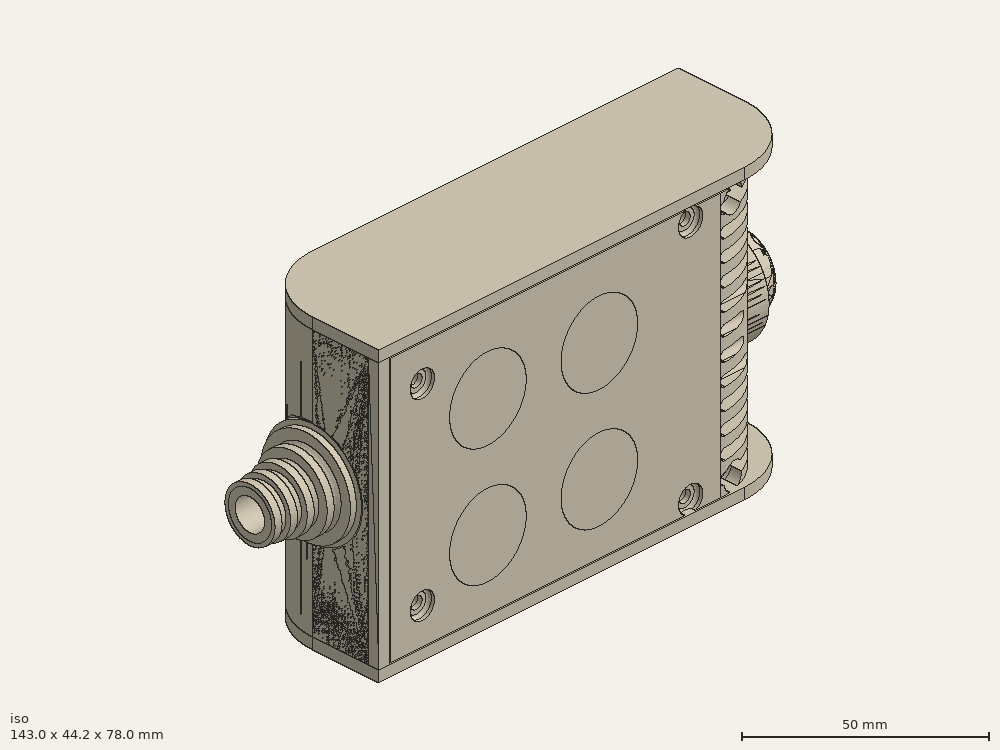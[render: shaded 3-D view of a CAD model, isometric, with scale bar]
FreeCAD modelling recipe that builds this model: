
FCSTD DOCUMENT  (FreeCAD 0.19R0.19.2)
Label: enclosure_126
License: All rights reserved
LicenseURL: http://en.wikipedia.org/wiki/All_rights_reserved
objects: Part::Feature×72, Part::Revolution×72, Part::MultiFuse×61, Sketcher::SketchObject×37, Part::Fillet×26, Part::Extrusion×25, Part::Cut×25, Part::Cylinder×22, Part::Box×12, App::MeasureDistance×4
note: 352 computed .brp shape members not serialized (recipe doc carries the construction recipe); baked Part::Feature solids carry a one-line shape summary decoded from their .brp

FEATURE [Sketcher::SketchObject] Sketch  label="topSketch"
  FullyConstrained = true
  sketch-geometry (20):
    g0: LineSegment StartX=5.58133e-06 StartY=3 StartZ=0 EndX=5.58133e-06 EndY=19 EndZ=0
    g1: ArcOfCircle CenterX=19 CenterY=19 CenterZ=0 NormalX=0 NormalY=0 NormalZ=1 AngleXU=0 Radius=19 StartAngle=1.5708 EndAngle=3.14159
    g2: ArcOfCircle CenterX=19 CenterY=19 CenterZ=0 NormalX=0 NormalY=0 NormalZ=1 AngleXU=0 Radius=16 StartAngle=1.5708 EndAngle=3.14159
    g3: LineSegment StartX=114 StartY=35 StartZ=0 EndX=19 EndY=35 EndZ=0
    g4: LineSegment StartX=5.58133e-06 StartY=3 StartZ=0 EndX=5.58133e-06 EndY=0 EndZ=0
    g5: LineSegment StartX=3.00001 StartY=0 StartZ=0 EndX=5.58133e-06 EndY=0 EndZ=0
    g6: LineSegment StartX=3.00001 StartY=19 StartZ=0 EndX=3.00001 EndY=0 EndZ=0
    g7: LineSegment StartX=19 StartY=38 StartZ=0 EndX=124 EndY=38 EndZ=0
    g8: LineSegment StartX=124 StartY=38 StartZ=0 EndX=124 EndY=19 EndZ=0
    g9: Circle CenterX=119 CenterY=35 CenterZ=0 NormalX=0 NormalY=0 NormalZ=1 AngleXU=0 Radius=1
    g10: Circle CenterX=121 CenterY=35 CenterZ=0 NormalX=0 NormalY=0 NormalZ=1 AngleXU=0 Radius=1
    g11: Circle CenterX=121 CenterY=33 CenterZ=0 NormalX=0 NormalY=0 NormalZ=1 AngleXU=0 Radius=1
    g12: BSplineCurve PolesCount=3 KnotsCount=2 Degree=2 IsPeriodic=0
    g13: GeomPoint X=119 Y=35 Z=0
    g14: GeomPoint X=121 Y=33 Z=0
    g15: LineSegment StartX=119 StartY=35 StartZ=0 EndX=114 EndY=35 EndZ=0
    g16: LineSegment StartX=121 StartY=33 StartZ=0 EndX=121 EndY=19 EndZ=0
    g17: ArcOfCircle CenterX=105 CenterY=19 CenterZ=0 NormalX=0 NormalY=0 NormalZ=1 AngleXU=0 Radius=19 StartAngle=5.7297 EndAngle=6.28319
    g18: ArcOfCircle CenterX=105 CenterY=19 CenterZ=0 NormalX=0 NormalY=0 NormalZ=1 AngleXU=0 Radius=16 StartAngle=5.60905 EndAngle=6.28319
    g19: LineSegment StartX=117.5 StartY=9.01251 StartZ=0 EndX=121.163 EndY=9.0125 EndZ=0
  constraints (44):
    c: Vertical(g0)
    c: Block(g0)
    c: Coincident(g1,g0)
    c: Block(g1)
    c: Coincident(g2,g1)
    c: Block(g2)
    c: Coincident(g3,g2)
    c: Horizontal(g3)
    c: Tangent(g3,g2)
    c: Coincident(g4,g0)
    c: Distance(g4) = 3
    c: Vertical(g4)
    c: Coincident(g5,g4)
    c: Horizontal(g5)
    c: Coincident(g6,g2)
    c: Coincident(g6,g5)
    c: Vertical(g6)
    c: Horizontal(g7)
    c: Distance(g7) = 105
    c: Coincident(g7,g1)
    c: Vertical(g8)
    c: Distance(g8) = 19
    c: Block(g3)
    c: Coincident(g8,g7)
    c: Weight(g9) = 1
    c: Equal(g9,g10)
    c: Equal(g9,g11)
    c: InternalAlignment(g9,g12)
    c: InternalAlignment(g10,g12)
    c: InternalAlignment(g11,g12)
    c: InternalAlignment(g13,g12)
    c: InternalAlignment(g14,g12)
    c: Block(g12)
    c: Coincident(g15,g12)
    c: Coincident(g15,g3)
    c: Horizontal(g15)
    c: Coincident(g16,g12)
    c: Vertical(g16)
    c: Distance(g16) = 14
    c: Block(g17)
    c: Coincident(g18,g17)
    c: Block(g18)
    c: Coincident(g19,g18)
    c: Coincident(g19,g17)
FEATURE [Sketcher::SketchObject] Sketch001  label="bottomSketch"
  FullyConstrained = true
  sketch-geometry (32):
    g0: LineSegment StartX=3.3 StartY=-6.03275e-07 StartZ=0 EndX=98 EndY=-6.03275e-07 EndZ=0
    g1: ArcOfCircle CenterX=98 CenterY=19 CenterZ=0 NormalX=0 NormalY=0 NormalZ=1 AngleXU=0 Radius=19 StartAngle=4.71239 EndAngle=5.71103
    g2: LineSegment StartX=6.3 StartY=8 StartZ=0 EndX=3.3 EndY=8 EndZ=0
    g3: LineSegment StartX=3.3 StartY=8 StartZ=0 EndX=3.3 EndY=-6.03275e-07 EndZ=0
    g4: ArcOfCircle CenterX=8.3 CenterY=5 CenterZ=0 NormalX=0 NormalY=0 NormalZ=1 AngleXU=0 Radius=2 StartAngle=3.14159 EndAngle=4.71239
    g5: LineSegment StartX=6.3 StartY=8 StartZ=0 EndX=6.3 EndY=5 EndZ=0
    g6: ArcOfCircle CenterX=98 CenterY=19 CenterZ=0 NormalX=0 NormalY=0 NormalZ=1 AngleXU=0 Radius=12.7 StartAngle=4.71239 EndAngle=6.28319
    g7: LineSegment StartX=94.7 StartY=3 StartZ=0 EndX=8.3 EndY=3 EndZ=0
    g8-g12: Circle x5 (B-spline internal-alignment scaffolding for g13; pole/knot coordinates omitted)
    g13: BSplineCurve PolesCount=5 KnotsCount=3 Degree=3 IsPeriodic=0
    g14: GeomPoint X=98 Y=6.3 Z=0
    g15: GeomPoint X=96.3938 Y=4.71946 Z=0
    g16: GeomPoint X=94.7 Y=3 Z=0
    g17-g23: Circle x7 (B-spline internal-alignment scaffolding for g24; pole/knot coordinates omitted)
    g24: BSplineCurve PolesCount=7 KnotsCount=5 Degree=3 IsPeriodic=0
    g25-g29: GeomPoint x5 (B-spline internal-alignment scaffolding for g24; pole/knot coordinates omitted)
    g30: ArcOfCircle CenterX=98 CenterY=19 CenterZ=0 NormalX=0 NormalY=0 NormalZ=1 AngleXU=0 Radius=15.7 StartAngle=5.81226 EndAngle=6.28319
    g31: LineSegment StartX=110.7 StartY=19 StartZ=0 EndX=113.7 EndY=19 EndZ=0
  constraints (41):
    c: Horizontal(g0)
    c: Coincident(g1,g0)
    c: Block(g1)
    c: Horizontal(g2)
    c: Distance(g2) = 3
    c: Coincident(g3,g2)
    c: Vertical(g3)
    c: Coincident(g3,g0)
    c: Block(g4)
    c: Block(g2)
    c: Coincident(g5,g2)
    c: Coincident(g5,g4)
    c: Vertical(g5)
    c: Coincident(g6,g1)
    c: Block(g6)
    c: Coincident(g7,g4)
    c: Horizontal(g7)
    c: Block(g0)
    c: Block(g7)
    c: Block(g3)
    c: Coincident(g13,g6)
    c: Weight(g8) = 1
    c: Equal(g8, g9-g12) x4
    c: Coincident(g13,g7)
    c: InternalAlignment(g8-g12 -> g13) x5
    c: InternalAlignment(g14,g13)
    c: InternalAlignment(g15,g13)
    c: InternalAlignment(g16,g13)
    c: Block(g13)
    c: Weight(g17) = 1
    c: Equal(g17, g18-g23) x6
    c: Coincident(g24,g1)
    c: InternalAlignment(g17-g23 -> g24) x7
    c: InternalAlignment(g25-g29 -> g24) x5
    c: Block(g24)
    c: Coincident(g30,g24)
    c: Coincident(g31,g6)
    c: Coincident(g31,g30)
    c: Horizontal(g31)
    c: Block(g31)
    c: Block(g30)
FEATURE [Part::Extrusion] Extrude  label="top"
  Base = -> Sketch
  Dir = (0,0,1)
  DirMode = 2
  FaceMakerClass = Part::FaceMakerBullseye
  LengthFwd = 72
  LengthRev = 0
  Solid = true
  Symmetric = false
FEATURE [Part::Extrusion] Extrude001  label="bottom"
  Base = -> Sketch001
  Dir = (0,0,1)
  DirMode = 2
  FaceMakerClass = Part::FaceMakerBullseye
  LengthFwd = 71.4
  LengthRev = 0
  Placement = pos=(0,0,0.3) rot=(0,0,1;0rad)
  Solid = true
  Symmetric = false
FEATURE [Sketcher::SketchObject] Sketch002  label="topSketch001"
  FullyConstrained = true
  sketch-geometry (6):
    g0: ArcOfCircle CenterX=19 CenterY=19 CenterZ=0 NormalX=0 NormalY=0 NormalZ=1 AngleXU=0 Radius=19 StartAngle=1.5708 EndAngle=3.14159
    g1: LineSegment StartX=5.22862e-06 StartY=19 StartZ=0 EndX=5.22862e-06 EndY=1.19904e-11 EndZ=0
    g2: LineSegment StartX=19 StartY=38 StartZ=0 EndX=124 EndY=38 EndZ=0
    g3: LineSegment StartX=5.22862e-06 StartY=1.19904e-11 StartZ=0 EndX=105 EndY=1.19904e-11 EndZ=0
    g4: ArcOfCircle CenterX=105 CenterY=19 CenterZ=0 NormalX=0 NormalY=0 NormalZ=1 AngleXU=0 Radius=19 StartAngle=4.71239 EndAngle=6.28319
    g5: LineSegment StartX=124 StartY=38 StartZ=0 EndX=124 EndY=19 EndZ=0
  constraints (16):
    c: Block(g0)
    c: Coincident(g1,g0)
    c: Vertical(g1)
    c: Horizontal(g2)
    c: Distance(g2) = 105
    c: Coincident(g2,g0)
    c: Distance(g1) = 19
    c: Coincident(g3,g1)
    c: Horizontal(g3)
    c: Distance(g3) = 105
    c: Block(g4)
    c: Coincident(g4,g3)
    c: Coincident(g5,g2)
    c: Coincident(g5,g4)
    c: Vertical(g5)
    c: Distance(g5) = 19
FEATURE [Part::Extrusion] Extrude002  label="sideA"
  Base = -> Sketch002
  Dir = (0,0,1)
  DirMode = 2
  FaceMakerClass = Part::FaceMakerBullseye
  LengthFwd = 3
  LengthRev = 0
  Placement = pos=(0,0,-3) rot=(0,0,1;0rad)
  Solid = true
  Symmetric = false
FEATURE [Sketcher::SketchObject] Sketch003  label="topSketch002"
  FullyConstrained = true
  sketch-geometry (6):
    g0: LineSegment StartX=19 StartY=38 StartZ=0 EndX=117 EndY=38 EndZ=0
    g1: ArcOfCircle CenterX=19 CenterY=19 CenterZ=0 NormalX=0 NormalY=0 NormalZ=1 AngleXU=0 Radius=19 StartAngle=1.5708 EndAngle=3.14159
    g2: LineSegment StartX=117 StartY=38 StartZ=0 EndX=117 EndY=19 EndZ=0
    g3: LineSegment StartX=98 StartY=1.0161e-12 StartZ=0 EndX=5.22862e-06 EndY=1.0161e-12 EndZ=0
    g4: LineSegment StartX=5.22862e-06 StartY=19 StartZ=0 EndX=5.22862e-06 EndY=1.0161e-12 EndZ=0
    g5: ArcOfCircle CenterX=98 CenterY=19 CenterZ=0 NormalX=0 NormalY=0 NormalZ=1 AngleXU=0 Radius=19 StartAngle=4.71239 EndAngle=6.28319
  constraints (16):
    c: Horizontal(g0)
    c: Distance(g0) = 98
    c: Coincident(g1,g0)
    c: Block(g1)
    c: Coincident(g2,g0)
    c: Vertical(g2)
    c: Distance(g2) = 19
    c: Horizontal(g3)
    c: Coincident(g4,g1)
    c: Vertical(g4)
    c: Coincident(g3,g4)
    c: Block(g3)
    c: Coincident(g5,g2)
    c: Coincident(g5,g3)
    c: Block(g0)
    c: Block(g5)
FEATURE [Sketcher::SketchObject] Sketch004
  FullyConstrained = true
  MapMode = 3
  Placement = pos=(0,0,0) rot=(1,0,0;1.5708rad)
  Support = -> [Extrude]
  sketch-geometry (8):
    g0: Circle CenterX=80.351 CenterY=-67.6202 CenterZ=0 NormalX=0 NormalY=0 NormalZ=1 AngleXU=0 Radius=2
    g1: Circle CenterX=80.351 CenterY=-67.6202 CenterZ=0 NormalX=0 NormalY=0 NormalZ=1 AngleXU=0 Radius=3
    g2: Circle CenterX=80.351 CenterY=-4.92017 CenterZ=0 NormalX=0 NormalY=0 NormalZ=1 AngleXU=0 Radius=2
    g3: Circle CenterX=80.351 CenterY=-4.92017 CenterZ=0 NormalX=0 NormalY=0 NormalZ=1 AngleXU=0 Radius=3
    g4: Circle CenterX=23.851 CenterY=-4.92017 CenterZ=0 NormalX=0 NormalY=0 NormalZ=1 AngleXU=0 Radius=2
    g5: Circle CenterX=23.851 CenterY=-4.92017 CenterZ=0 NormalX=0 NormalY=0 NormalZ=1 AngleXU=0 Radius=3
    g6: Circle CenterX=23.851 CenterY=-67.6202 CenterZ=0 NormalX=0 NormalY=0 NormalZ=1 AngleXU=0 Radius=2
    g7: Circle CenterX=23.851 CenterY=-67.6202 CenterZ=0 NormalX=0 NormalY=0 NormalZ=1 AngleXU=0 Radius=3
  constraints (8):
    c: Block(g3)
    c: Block(g2)
    c: Block(g1)
    c: Block(g0)
    c: Block(g6)
    c: Block(g7)
    c: Block(g4)
    c: Block(g5)
FEATURE [Part::Extrusion] Extrude004
  Base = -> Sketch004
  Dir = (0,-1,2e-16)
  DirMode = 2
  FaceMakerClass = Part::FaceMakerBullseye
  LengthFwd = 6
  LengthRev = 0
  Placement = pos=(0,9,0) rot=(0,0,1;0rad)
  Solid = true
  Symmetric = false
FEATURE [Sketcher::SketchObject] Sketch005
  FullyConstrained = true
  MapMode = 3
  Placement = pos=(0,0,0) rot=(1,0,0;1.5708rad)
  Support = -> [Extrude]
  sketch-geometry (8):
    g0: Circle CenterX=80.351 CenterY=-67.6202 CenterZ=0 NormalX=0 NormalY=0 NormalZ=1 AngleXU=0 Radius=3
    g1: Circle CenterX=80.351 CenterY=-4.92017 CenterZ=0 NormalX=0 NormalY=0 NormalZ=1 AngleXU=0 Radius=3
    g2: Circle CenterX=23.851 CenterY=-4.92017 CenterZ=0 NormalX=0 NormalY=0 NormalZ=1 AngleXU=0 Radius=3
    g3: Circle CenterX=23.851 CenterY=-67.6202 CenterZ=0 NormalX=0 NormalY=0 NormalZ=1 AngleXU=0 Radius=3
    g4: Circle CenterX=23.851 CenterY=-67.6202 CenterZ=0 NormalX=0 NormalY=0 NormalZ=1 AngleXU=0 Radius=5
    g5: Circle CenterX=80.351 CenterY=-67.6202 CenterZ=0 NormalX=0 NormalY=0 NormalZ=1 AngleXU=0 Radius=5
    g6: Circle CenterX=23.851 CenterY=-4.92017 CenterZ=0 NormalX=0 NormalY=0 NormalZ=1 AngleXU=0 Radius=5
    g7: Circle CenterX=80.351 CenterY=-4.92017 CenterZ=0 NormalX=0 NormalY=0 NormalZ=1 AngleXU=0 Radius=5
  constraints (8):
    c: Block(g1)
    c: Block(g0)
    c: Block(g3)
    c: Block(g2)
    c: Block(g5)
    c: Block(g4)
    c: Block(g6)
    c: Block(g7)
FEATURE [Part::Extrusion] Extrude005
  Base = -> Sketch005
  Dir = (0,-1,2e-16)
  DirMode = 2
  FaceMakerClass = Part::FaceMakerBullseye
  LengthFwd = 2
  LengthRev = 0
  Solid = true
  Symmetric = false
FEATURE [Sketcher::SketchObject] Sketch006
  FullyConstrained = true
  MapMode = 3
  Placement = pos=(0,0,0) rot=(1,0,0;1.5708rad)
  sketch-geometry (8):
    g0: Circle CenterX=80.351 CenterY=-67.6202 CenterZ=0 NormalX=0 NormalY=0 NormalZ=1 AngleXU=0 Radius=3
    g1: Circle CenterX=80.351 CenterY=-4.92017 CenterZ=0 NormalX=0 NormalY=0 NormalZ=1 AngleXU=0 Radius=3
    g2: Circle CenterX=23.851 CenterY=-4.92017 CenterZ=0 NormalX=0 NormalY=0 NormalZ=1 AngleXU=0 Radius=3
    g3: Circle CenterX=23.851 CenterY=-67.6202 CenterZ=0 NormalX=0 NormalY=0 NormalZ=1 AngleXU=0 Radius=3
    g4: Circle CenterX=23.851 CenterY=-67.6202 CenterZ=0 NormalX=0 NormalY=0 NormalZ=1 AngleXU=0 Radius=5
    g5: Circle CenterX=80.351 CenterY=-67.6202 CenterZ=0 NormalX=0 NormalY=0 NormalZ=1 AngleXU=0 Radius=5
    g6: Circle CenterX=23.851 CenterY=-4.92017 CenterZ=0 NormalX=0 NormalY=0 NormalZ=1 AngleXU=0 Radius=5
    g7: Circle CenterX=80.351 CenterY=-4.92017 CenterZ=0 NormalX=0 NormalY=0 NormalZ=1 AngleXU=0 Radius=5
  constraints (8):
    c: Block(g1)
    c: Block(g0)
    c: Block(g3)
    c: Block(g2)
    c: Block(g5)
    c: Block(g4)
    c: Block(g6)
    c: Block(g7)
FEATURE [Part::Extrusion] Extrude007
  Base = -> Sketch006
  Dir = (0,-1,2e-16)
  DirMode = 2
  FaceMakerClass = Part::FaceMakerBullseye
  LengthFwd = 2
  LengthRev = 0
  Solid = true
  Symmetric = false
FEATURE [Part::Fillet] Fillet
  Base = -> Extrude007
  Edges = 4 edges r=1.99: [Edge6,Edge12,Edge18,Edge24]
FEATURE [Part::Cut] Cut
  Base = -> Extrude005
  Placement = pos=(0,5,0) rot=(0,0,1;0rad)
  Tool = -> Fillet
FEATURE [Part::MultiFuse] Fusion  label="pCBScrews"
  Placement = pos=(-2.5,0,72.3) rot=(0,0,1;0rad)
  Shapes = -> [Extrude004,Cut]
FEATURE [App::MeasureDistance] Distance  label="Distance: 0.69 mm"
  Distance = 0.685967
  P1 = (24.0138,2.9647,0.3)
  P2 = (23.8901,3,-0.373787)
FEATURE [App::MeasureDistance] Distance001  label="Distance: 0.53 mm"
  Distance = 0.533607
  P1 = (80.2939,3,72.2334)
  P2 = (80.281,2.99661,71.7)
FEATURE [Part::Fillet] Fillet001
  Base = -> Extrude001
  Edges = 1 edges r=2.4: [Edge17]
FEATURE [Part::Fillet] Fillet002  label="bottom001"
  Base = -> Fillet001
  Edges = 1 edges r=2.4: [Edge36]
FEATURE [Part::Fillet] Fillet003  label="top001"
  Base = -> Extrude
  Edges = 1 edges r=2: [Edge1]
FEATURE [Sketcher::SketchObject] Sketch007
  FullyConstrained = true
  sketch-geometry (16):
    g0: LineSegment StartX=4 StartY=0 StartZ=0 EndX=4 EndY=2.4 EndZ=0
    g1: LineSegment StartX=4 StartY=2.4 StartZ=0 EndX=7 EndY=2.4 EndZ=0
    g2: LineSegment StartX=4 StartY=0 StartZ=0 EndX=5.7 EndY=0 EndZ=0
    g3: LineSegment StartX=5.7 StartY=0 StartZ=0 EndX=5.7 EndY=-5.6 EndZ=0
    g4-g8: Circle x5 (B-spline internal-alignment scaffolding for g9; pole/knot coordinates omitted)
    g9: BSplineCurve PolesCount=5 KnotsCount=3 Degree=3 IsPeriodic=0
    g10: GeomPoint X=7 Y=2.4 Z=0
    g11: GeomPoint X=10.4582 Y=-1.55472 Z=0
    g12: GeomPoint X=14 Y=-5.6 Z=0
    g13: LineSegment StartX=14 StartY=-5.6 StartZ=0 EndX=14 EndY=-14.1 EndZ=0
    g14: LineSegment StartX=14 StartY=-14.1 StartZ=0 EndX=6.5 EndY=-14.1 EndZ=0
    g15: LineSegment StartX=5.7 StartY=-5.6 StartZ=0 EndX=6.5 EndY=-14.1 EndZ=0
  constraints (28):
    c: Distance(g0) = 2.4
    c: Vertical(g0)
    c: Block(g0)
    c: Coincident(g1,g0)
    c: Horizontal(g1)
    c: Distance(g1) = 3
    c: Coincident(g2,g0)
    c: Horizontal(g2)
    c: Distance(g2) = 1.7
    c: Coincident(g3,g2)
    c: Vertical(g3)
    c: Distance(g3) = 5.6
    c: Coincident(g9,g1)
    c: Weight(g4) = 1
    c: Equal(g4, g5-g8) x4
    c: InternalAlignment(g4-g8 -> g9) x5
    c: InternalAlignment(g10,g9)
    c: InternalAlignment(g11,g9)
    c: InternalAlignment(g12,g9)
    c: Block(g9)
    c: Coincident(g13,g9)
    c: Vertical(g13)
    c: Distance(g13) = 8.5
    c: Coincident(g14,g13)
    c: Horizontal(g14)
    c: Distance(g14) = 7.5
    c: Coincident(g15,g3)
    c: Coincident(g15,g14)
FEATURE [Part::Feature] Face
  shape: bbox 10 x 16.5 x 2e-07 mm, 1 faces, 0 solids (baked)
FEATURE [Part::Revolution] Revolve  label="plugHousing"
  Angle = 360
  Axis = (0,1,0)
  Base = (0,0,0)
  FaceMakerClass = Part::FaceMakerBullseye
  Placement = pos=(0,0,36.15) rot=(0,0,1;0rad)
  Solid = false
  Source = -> Face
  Symmetric = false
FEATURE [Part::Feature] Face001
  shape: bbox 10 x 16.5 x 2e-07 mm, 1 faces, 0 solids (baked)
FEATURE [Part::Revolution] Revolve001  label="plugHousing001"
  Angle = 360
  Axis = (0,1,0)
  Base = (0,0,0)
  FaceMakerClass = Part::FaceMakerBullseye
  Placement = pos=(0,0,36.15) rot=(0,0,1;0rad)
  Solid = false
  Source = -> Face001
  Symmetric = false
FEATURE [Part::MultiFuse] Fusion001  label="plugHousing002"
  Placement = pos=(0,0,0) rot=(0,0,1;1.5708rad)
  Shapes = -> [Revolve001,Revolve]
FEATURE [Part::Feature] Face002
  shape: bbox 10 x 16.5 x 2e-07 mm, 1 faces, 0 solids (baked)
FEATURE [Part::Revolution] Revolve003  label="plugHousing005"
  Angle = 360
  Axis = (0,1,0)
  Base = (0,0,0)
  FaceMakerClass = Part::FaceMakerBullseye
  Placement = pos=(0,0,36.15) rot=(0,0,1;0rad)
  Solid = false
  Source = -> Face002
  Symmetric = false
FEATURE [Part::Feature] Face003
  shape: bbox 10 x 16.5 x 2e-07 mm, 1 faces, 0 solids (baked)
FEATURE [Part::Revolution] Revolve002  label="plugHousing003"
  Angle = 360
  Axis = (0,1,0)
  Base = (0,0,0)
  FaceMakerClass = Part::FaceMakerBullseye
  Placement = pos=(0,0,36.15) rot=(0,0,1;0rad)
  Solid = false
  Source = -> Face003
  Symmetric = false
FEATURE [Part::MultiFuse] Fusion002  label="plugHousing004"
  Placement = pos=(0,0,0) rot=(0,0,1;1.5708rad)
  Shapes = -> [Revolve002,Revolve003]
FEATURE [Part::MultiFuse] Fusion003  label="plugHousing006"
  Placement = pos=(0,19,0) rot=(0,0,1;3.14159rad)
  Shapes = -> [Fusion002,Fusion001]
FEATURE [Part::Feature] Face004
  shape: bbox 10 x 16.5 x 2e-07 mm, 1 faces, 0 solids (baked)
FEATURE [Part::Revolution] Revolve006  label="plugHousing010"
  Angle = 360
  Axis = (0,1,0)
  Base = (0,0,0)
  FaceMakerClass = Part::FaceMakerBullseye
  Placement = pos=(0,0,36.15) rot=(0,0,1;0rad)
  Solid = false
  Source = -> Face004
  Symmetric = false
FEATURE [Part::Feature] Face005
  shape: bbox 10 x 16.5 x 2e-07 mm, 1 faces, 0 solids (baked)
FEATURE [Part::Revolution] Revolve007  label="plugHousing011"
  Angle = 360
  Axis = (0,1,0)
  Base = (0,0,0)
  FaceMakerClass = Part::FaceMakerBullseye
  Placement = pos=(0,0,36.15) rot=(0,0,1;0rad)
  Solid = false
  Source = -> Face005
  Symmetric = false
FEATURE [Part::Feature] Face006
  shape: bbox 10 x 16.5 x 2e-07 mm, 1 faces, 0 solids (baked)
FEATURE [Part::Revolution] Revolve004  label="plugHousing007"
  Angle = 360
  Axis = (0,1,0)
  Base = (0,0,0)
  FaceMakerClass = Part::FaceMakerBullseye
  Placement = pos=(0,0,36.15) rot=(0,0,1;0rad)
  Solid = false
  Source = -> Face006
  Symmetric = false
FEATURE [Part::MultiFuse] Fusion004  label="plugHousing009"
  Placement = pos=(0,0,0) rot=(0,0,1;1.5708rad)
  Shapes = -> [Revolve004,Revolve007]
FEATURE [Part::Feature] Face007
  shape: bbox 10 x 16.5 x 2e-07 mm, 1 faces, 0 solids (baked)
FEATURE [Part::Revolution] Revolve005  label="plugHousing008"
  Angle = 360
  Axis = (0,1,0)
  Base = (0,0,0)
  FaceMakerClass = Part::FaceMakerBullseye
  Placement = pos=(0,0,36.15) rot=(0,0,1;0rad)
  Solid = false
  Source = -> Face007
  Symmetric = false
FEATURE [Part::MultiFuse] Fusion005  label="plugHousing012"
  Placement = pos=(0,0,0) rot=(0,0,1;1.5708rad)
  Shapes = -> [Revolve006,Revolve005]
FEATURE [Part::MultiFuse] Fusion006  label="plugHousing013"
  Placement = pos=(0,19,0) rot=(0,0,1;3.14159rad)
  Shapes = -> [Fusion005,Fusion004]
FEATURE [Part::MultiFuse] Fusion007  label="plugHousing014"
  Placement = pos=(122.621,0,-0.15) rot=(0,0,1;0rad)
  Shapes = -> [Fusion003,Fusion006]
FEATURE [Part::Cylinder] Cylinder002
  Angle = 360
  AttacherType = Attacher::AttachEngine3D
  Height = 20
  Placement = pos=(0,0,36.15) rot=(0,0,1;0rad)
  Radius = 4
FEATURE [Part::Cylinder] Cylinder003
  Angle = 360
  AttacherType = Attacher::AttachEngine3D
  Height = 10
  Placement = pos=(0,0,36.15) rot=(0,0,1;0rad)
  Radius = 4
FEATURE [Part::MultiFuse] Fusion009  label="removeToCreateHoleForPlugHousing"
  Placement = pos=(70,19,36.15) rot=(0,1,0;1.5708rad)
  Shapes = -> [Cylinder002,Cylinder003]
FEATURE [Part::Cylinder] Cylinder004
  Angle = 360
  AttacherType = Attacher::AttachEngine3D
  Height = 20
  Placement = pos=(0,0,36.15) rot=(0,0,1;0rad)
  Radius = 4
FEATURE [Part::Cylinder] Cylinder005
  Angle = 360
  AttacherType = Attacher::AttachEngine3D
  Height = 10
  Placement = pos=(0,0,36.15) rot=(0,0,1;0rad)
  Radius = 4
FEATURE [Part::MultiFuse] Fusion010  label="removeToCreateHoleForPlugHousing001"
  Placement = pos=(70,19,36.15) rot=(0,1,0;1.5708rad)
  Shapes = -> [Cylinder004,Cylinder005]
FEATURE [Part::Cut] Cut001
  Base = -> Fillet003
  Tool = -> Fusion010
FEATURE [Part::Cut] Cut002  label="Bottom"
  Base = -> Fillet002
  Tool = -> Fusion009
FEATURE [Part::Feature] Face008
  shape: bbox 10 x 16.5 x 2e-07 mm, 1 faces, 0 solids (baked)
FEATURE [Part::Revolution] Revolve011  label="plugHousing021"
  Angle = 360
  Axis = (0,1,0)
  Base = (0,0,0)
  FaceMakerClass = Part::FaceMakerBullseye
  Placement = pos=(0,0,36.15) rot=(0,0,1;0rad)
  Solid = false
  Source = -> Face008
  Symmetric = false
FEATURE [Part::Feature] Face009
  shape: bbox 10 x 16.5 x 2e-07 mm, 1 faces, 0 solids (baked)
FEATURE [Part::Revolution] Revolve012  label="plugHousing022"
  Angle = 360
  Axis = (0,1,0)
  Base = (0,0,0)
  FaceMakerClass = Part::FaceMakerBullseye
  Placement = pos=(0,0,36.15) rot=(0,0,1;0rad)
  Solid = false
  Source = -> Face009
  Symmetric = false
FEATURE [Part::Feature] Face010 .. Face013  x4 (patterned run collapsed; names and placements below)
  shape: bbox 10 x 16.5 x 2e-07 mm, 1 faces, 0 solids (baked)
FEATURE [Part::Revolution] Revolve015  label="plugHousing027"
  Angle = 360
  Axis = (0,1,0)
  Base = (0,0,0)
  FaceMakerClass = Part::FaceMakerBullseye
  Placement = pos=(0,0,36.15) rot=(0,0,1;0rad)
  Solid = false
  Source = -> Face013
  Symmetric = false
FEATURE [Part::Feature] Face014
  shape: bbox 10 x 16.5 x 2e-07 mm, 1 faces, 0 solids (baked)
FEATURE [Part::Feature] Face015
  shape: bbox 10 x 16.5 x 2e-07 mm, 1 faces, 0 solids (baked)
FEATURE [Part::Feature] Face016
  shape: bbox 10 x 16.5 x 2e-07 mm, 1 faces, 0 solids (baked)
FEATURE [Part::Revolution] Revolve019  label="plugHousing033"
  Angle = 360
  Axis = (0,1,0)
  Base = (0,0,0)
  FaceMakerClass = Part::FaceMakerBullseye
  Placement = pos=(0,0,36.15) rot=(0,0,1;0rad)
  Solid = false
  Source = -> Face016
  Symmetric = false
FEATURE [Part::Feature] Face017
  shape: bbox 10 x 16.5 x 2e-07 mm, 1 faces, 0 solids (baked)
FEATURE [Part::Revolution] Revolve020  label="plugHousing034"
  Angle = 360
  Axis = (0,1,0)
  Base = (0,0,0)
  FaceMakerClass = Part::FaceMakerBullseye
  Placement = pos=(0,0,36.15) rot=(0,0,1;0rad)
  Solid = false
  Source = -> Face017
  Symmetric = false
FEATURE [Part::Feature] Face018
  shape: bbox 10 x 16.5 x 2e-07 mm, 1 faces, 0 solids (baked)
FEATURE [Part::Revolution] Revolve016  label="plugHousing030"
  Angle = 360
  Axis = (0,1,0)
  Base = (0,0,0)
  FaceMakerClass = Part::FaceMakerBullseye
  Placement = pos=(0,0,36.15) rot=(0,0,1;0rad)
  Solid = false
  Source = -> Face018
  Symmetric = false
FEATURE [Part::MultiFuse] Fusion020  label="plugHousing038"
  Placement = pos=(0,0,0) rot=(0,0,1;1.5708rad)
  Shapes = -> [Revolve016,Revolve020]
FEATURE [Part::Feature] Face019
  shape: bbox 10 x 16.5 x 2e-07 mm, 1 faces, 0 solids (baked)
FEATURE [Part::Feature] Face020
  shape: bbox 10 x 16.5 x 2e-07 mm, 1 faces, 0 solids (baked)
FEATURE [Part::Revolution] Revolve017  label="plugHousing031"
  Angle = 360
  Axis = (0,1,0)
  Base = (0,0,0)
  FaceMakerClass = Part::FaceMakerBullseye
  Placement = pos=(0,0,36.15) rot=(0,0,1;0rad)
  Solid = false
  Source = -> Face020
  Symmetric = false
FEATURE [Part::MultiFuse] Fusion021  label="plugHousing039"
  Placement = pos=(0,0,0) rot=(0,0,1;1.5708rad)
  Shapes = -> [Revolve019,Revolve017]
FEATURE [Part::MultiFuse] Fusion023  label="plugHousing041"
  Placement = pos=(0,19,0) rot=(0,0,1;3.14159rad)
  Shapes = -> [Fusion021,Fusion020]
FEATURE [Part::Revolution] Revolve022  label="plugHousing043"
  Angle = 360
  Axis = (0,1,0)
  Base = (0,0,0)
  FaceMakerClass = Part::FaceMakerBullseye
  Placement = pos=(0,0,36.15) rot=(0,0,1;0rad)
  Solid = false
  Source = -> Face019
  Symmetric = false
FEATURE [Part::Feature] Face021
  shape: bbox 10 x 16.5 x 2e-07 mm, 1 faces, 0 solids (baked)
FEATURE [Part::Revolution] Revolve023  label="plugHousing044"
  Angle = 360
  Axis = (0,1,0)
  Base = (0,0,0)
  FaceMakerClass = Part::FaceMakerBullseye
  Placement = pos=(0,0,36.15) rot=(0,0,1;0rad)
  Solid = false
  Source = -> Face021
  Symmetric = false
FEATURE [Part::Feature] Face022
  shape: bbox 10 x 16.5 x 2e-07 mm, 1 faces, 0 solids (baked)
FEATURE [Part::Revolution] Revolve018  label="plugHousing032"
  Angle = 360
  Axis = (0,1,0)
  Base = (0,0,0)
  FaceMakerClass = Part::FaceMakerBullseye
  Placement = pos=(0,0,36.15) rot=(0,0,1;0rad)
  Solid = false
  Source = -> Face022
  Symmetric = false
FEATURE [Part::MultiFuse] Fusion022  label="plugHousing040"
  Placement = pos=(0,0,0) rot=(0,0,1;1.5708rad)
  Shapes = -> [Revolve018,Revolve023]
FEATURE [Part::Feature] Face023
  shape: bbox 10 x 16.5 x 2e-07 mm, 1 faces, 0 solids (baked)
FEATURE [Part::Revolution] Revolve021  label="plugHousing035"
  Angle = 360
  Axis = (0,1,0)
  Base = (0,0,0)
  FaceMakerClass = Part::FaceMakerBullseye
  Placement = pos=(0,0,36.15) rot=(0,0,1;0rad)
  Solid = false
  Source = -> Face023
  Symmetric = false
FEATURE [Part::MultiFuse] Fusion018  label="plugHousing036"
  Placement = pos=(0,0,0) rot=(0,0,1;1.5708rad)
  Shapes = -> [Revolve022,Revolve021]
FEATURE [Part::MultiFuse] Fusion019  label="plugHousing037"
  Placement = pos=(0,19,0) rot=(0,0,1;3.14159rad)
  Shapes = -> [Fusion018,Fusion022]
FEATURE [Part::MultiFuse] Fusion024  label="plugHousing042"
  Placement = pos=(122.621,0,-0.15) rot=(0,0,1;0rad)
  Shapes = -> [Fusion023,Fusion019]
FEATURE [Part::Cylinder] Cylinder006
  Angle = 360
  AttacherType = Attacher::AttachEngine3D
  Height = 20
  Placement = pos=(0,0,36.15) rot=(0,0,1;0rad)
  Radius = 14.3
FEATURE [Part::Cylinder] Cylinder007
  Angle = 360
  AttacherType = Attacher::AttachEngine3D
  Height = 10
  Placement = pos=(0,0,36.15) rot=(0,0,1;0rad)
  Radius = 4
FEATURE [Part::MultiFuse] Fusion026  label="removeToCreteHoleForPlugHousing"
  Placement = pos=(70,19,36) rot=(0,1,0;1.5708rad)
  Shapes = -> [Cylinder006,Cylinder007]
FEATURE [Part::Box] Box001  label="Cube001"
  AttacherType = Attacher::AttachEngine3D
  Height = 28
  Length = 3
  Placement = pos=(110.7,19,22) rot=(0,0,1;0rad)
  Width = 15.7
FEATURE [Part::Cut] Cut003  label="top002"
  Base = -> Cut001
  Tool = -> Fusion007
FEATURE [Part::Revolution] Revolve008  label="plugHousing015"
  Angle = 360
  Axis = (0,1,0)
  Base = (0,0,0)
  FaceMakerClass = Part::FaceMakerBullseye
  Placement = pos=(0,0,36.15) rot=(0,0,1;0rad)
  Solid = false
  Source = -> Face010
  Symmetric = false
FEATURE [Part::MultiFuse] Fusion013  label="plugHousing020"
  Placement = pos=(0,0,0) rot=(0,0,1;1.5708rad)
  Shapes = -> [Revolve008,Revolve012]
FEATURE [Part::Cut] Cut004  label="top003"
  Base = -> Cut003
  Placement = pos=(1,0,0) rot=(0,0,1;0rad)
  Tool = -> Fusion026
FEATURE [Part::Cylinder] Cylinder008
  Angle = 360
  AttacherType = Attacher::AttachEngine3D
  Height = 20
  Placement = pos=(0,0,36.15) rot=(0,0,1;0rad)
  Radius = 10.3
FEATURE [Part::Cylinder] Cylinder009
  Angle = 360
  AttacherType = Attacher::AttachEngine3D
  Height = 10
  Placement = pos=(0,0,36.15) rot=(0,0,1;0rad)
  Radius = 4
FEATURE [Part::MultiFuse] Fusion027  label="removeToCreteHoleForPlugHousing001"
  Placement = pos=(70,19,36) rot=(0,1,0;1.5708rad)
  Shapes = -> [Cylinder008,Cylinder009]
FEATURE [Part::Cut] Cut005  label="plugHousingTab"
  Base = -> Box001
  Tool = -> Fusion027
FEATURE [Part::MultiFuse] Fusion028  label="plugHousing045"
  Shapes = -> [Fusion024,Cut005]
FEATURE [Part::Box] Box002  label="Cube002"
  AttacherType = Attacher::AttachEngine3D
  Height = 28.8
  Length = 3
  Placement = pos=(107.3,28,21.6) rot=(0,0,1;0rad)
  Width = 7
FEATURE [Part::Box] Box003  label="Cube003"
  AttacherType = Attacher::AttachEngine3D
  Height = 3
  Length = 6.4
  Placement = pos=(107.3,28,18.6) rot=(0,0,1;0rad)
  Width = 7
FEATURE [Part::Box] Box004  label="Cube004"
  AttacherType = Attacher::AttachEngine3D
  Height = 3
  Length = 6.4
  Placement = pos=(107.3,28,50.4) rot=(0,0,1;0rad)
  Width = 7
FEATURE [Part::MultiFuse] Fusion029  label="plugHousingBracketHolder"
  Shapes = -> [Box004,Box002,Box003]
FEATURE [Part::Cylinder] Cylinder010
  Angle = 360
  AttacherType = Attacher::AttachEngine3D
  Height = 20
  Placement = pos=(0,0,36.15) rot=(0,0,1;0rad)
  Radius = 14.3
FEATURE [Part::Cylinder] Cylinder011
  Angle = 360
  AttacherType = Attacher::AttachEngine3D
  Height = 10
  Placement = pos=(0,0,36.15) rot=(0,0,1;0rad)
  Radius = 4
FEATURE [Part::MultiFuse] Fusion030  label="removeToCreteHoleForPlugHousing002"
  Placement = pos=(70,19,36) rot=(0,1,0;1.5708rad)
  Shapes = -> [Cylinder010,Cylinder011]
FEATURE [Part::Cut] Cut006  label="plugHousingBracketHolder001"
  Base = -> Fusion029
  Tool = -> Fusion030
FEATURE [Part::Cylinder] Cylinder012
  Angle = 360
  AttacherType = Attacher::AttachEngine3D
  Height = 20
  Placement = pos=(0,0,36.15) rot=(0,0,1;0rad)
  Radius = 7
FEATURE [Part::Cylinder] Cylinder013
  Angle = 360
  AttacherType = Attacher::AttachEngine3D
  Height = 10
  Placement = pos=(0,0,36.15) rot=(0,0,1;0rad)
  Radius = 4
FEATURE [Part::MultiFuse] Fusion032  label="removeToCreteHoleForPlugHousing003"
  Placement = pos=(70,19,36) rot=(0,1,0;1.5708rad)
  Shapes = -> [Cylinder012,Cylinder013]
FEATURE [Part::Cut] Cut007  label="bottom002"
  Base = -> Cut002
  Tool = -> Fusion032
FEATURE [Sketcher::SketchObject] Sketch008
  FullyConstrained = true
  sketch-geometry (54):
    g0: LineSegment StartX=-4.2 StartY=0 StartZ=0 EndX=-6.2 EndY=0 EndZ=0
    g1: LineSegment StartX=-14 StartY=-18 StartZ=0 EndX=-14 EndY=-26.5 EndZ=0
    g2: LineSegment StartX=-4.2 StartY=0 StartZ=0 EndX=-4.2 EndY=-13.4877 EndZ=0
    g3: Circle CenterX=-4.2 CenterY=-13.4877 CenterZ=0 NormalX=0 NormalY=0 NormalZ=1 AngleXU=0 Radius=1
    g4: Circle CenterX=-4.2 CenterY=-26.5 CenterZ=0 NormalX=0 NormalY=0 NormalZ=1 AngleXU=0 Radius=1
    g5: Circle CenterX=-8.2 CenterY=-26.5 CenterZ=0 NormalX=0 NormalY=0 NormalZ=1 AngleXU=0 Radius=1
    g6: BSplineCurve PolesCount=3 KnotsCount=2 Degree=2 IsPeriodic=0
    g7: GeomPoint X=-4.2 Y=-13.4877 Z=0
    g8: GeomPoint X=-8.2 Y=-26.5 Z=0
    g9: LineSegment StartX=-14 StartY=-26.5 StartZ=0 EndX=-8.2 EndY=-26.5 EndZ=0
    g10: LineSegment StartX=-10.15 StartY=-12 StartZ=0 EndX=-10.15 EndY=-14 EndZ=0
    g11: LineSegment StartX=-12.8401 StartY=-16 StartZ=0 EndX=-10.1571 EndY=-16 EndZ=0
    g12: LineSegment StartX=-10.15 StartY=-14 StartZ=0 EndX=-8.70761 EndY=-14 EndZ=0
    g13: LineSegment StartX=-12.8401 StartY=-16 StartZ=0 EndX=-12.8401 EndY=-17.6958 EndZ=0
    g14: LineSegment StartX=-10.15 StartY=-12 StartZ=0 EndX=-7.79258 EndY=-12 EndZ=0
    g15: Circle CenterX=-6.2215 CenterY=-2 CenterZ=0 NormalX=0 NormalY=0 NormalZ=1 AngleXU=0 Radius=1
    g16: Circle CenterX=-6.22762 CenterY=-2.58724 CenterZ=0 NormalX=0 NormalY=0 NormalZ=1 AngleXU=0 Radius=1
    g17: Circle CenterX=-6.32538 CenterY=-4 CenterZ=0 NormalX=0 NormalY=0 NormalZ=1 AngleXU=0 Radius=1
    g18: BSplineCurve PolesCount=3 KnotsCount=2 Degree=2 IsPeriodic=0
    g19: GeomPoint X=-6.2215 Y=-2 Z=0
    g20: GeomPoint X=-6.32538 Y=-4 Z=0
    g21: Circle CenterX=-6.48644 CenterY=-5.99526 CenterZ=0 NormalX=0 NormalY=0 NormalZ=1 AngleXU=0 Radius=1
    g22: Circle CenterX=-6.58486 CenterY=-6.99526 CenterZ=0 NormalX=0 NormalY=0 NormalZ=1 AngleXU=0 Radius=1
    g23: Circle CenterX=-6.77343 CenterY=-8 CenterZ=0 NormalX=0 NormalY=0 NormalZ=1 AngleXU=0 Radius=1
    g24: BSplineCurve PolesCount=3 KnotsCount=2 Degree=2 IsPeriodic=0
    g25: GeomPoint X=-6.48644 Y=-5.99526 Z=0
    g26: GeomPoint X=-6.77343 Y=-8 Z=0
    g27: Circle CenterX=-7.19003 CenterY=-10 CenterZ=0 NormalX=0 NormalY=0 NormalZ=1 AngleXU=0 Radius=1
    g28: Circle CenterX=-7.44407 CenterY=-11.0915 CenterZ=0 NormalX=0 NormalY=0 NormalZ=1 AngleXU=0 Radius=1
    g29: Circle CenterX=-7.79258 CenterY=-12 CenterZ=0 NormalX=0 NormalY=0 NormalZ=1 AngleXU=0 Radius=1
    g30: BSplineCurve PolesCount=3 KnotsCount=2 Degree=2 IsPeriodic=0
    g31: GeomPoint X=-7.19003 Y=-10 Z=0
    g32: GeomPoint X=-7.79258 Y=-12 Z=0
    g33: Circle CenterX=-8.70761 CenterY=-14 CenterZ=0 NormalX=0 NormalY=0 NormalZ=1 AngleXU=0 Radius=1
    g34: Circle CenterX=-9.33087 CenterY=-15.1837 CenterZ=0 NormalX=0 NormalY=0 NormalZ=1 AngleXU=0 Radius=1
    g35: Circle CenterX=-10.1571 CenterY=-16 CenterZ=0 NormalX=0 NormalY=0 NormalZ=1 AngleXU=0 Radius=1
    g36: BSplineCurve PolesCount=3 KnotsCount=2 Degree=2 IsPeriodic=0
    g37: GeomPoint X=-8.70761 Y=-14 Z=0
    g38: GeomPoint X=-10.1571 Y=-16 Z=0
    g39: Circle CenterX=-12.8401 CenterY=-17.6958 CenterZ=0 NormalX=0 NormalY=0 NormalZ=1 AngleXU=0 Radius=1
    g40: Circle CenterX=-13.3521 CenterY=-17.9027 CenterZ=0 NormalX=0 NormalY=0 NormalZ=1 AngleXU=0 Radius=1
    g41: Circle CenterX=-14 CenterY=-18 CenterZ=0 NormalX=0 NormalY=0 NormalZ=1 AngleXU=0 Radius=1
    g42: BSplineCurve PolesCount=3 KnotsCount=2 Degree=2 IsPeriodic=0
    g43: GeomPoint X=-12.8401 Y=-17.6958 Z=0
    g44: GeomPoint X=-14 Y=-18 Z=0
    g45: LineSegment StartX=-6.2 StartY=0 StartZ=0 EndX=-7.2 EndY=0 EndZ=0
    g46: LineSegment StartX=-7.2 StartY=0 StartZ=0 EndX=-7.2 EndY=-2 EndZ=0
    g47: LineSegment StartX=-7.2 StartY=-2 StartZ=0 EndX=-6.2215 EndY=-2 EndZ=0
    g48: LineSegment StartX=-6.32538 StartY=-4 StartZ=0 EndX=-7.65538 EndY=-4 EndZ=0
    g49: LineSegment StartX=-7.65538 StartY=-4 StartZ=0 EndX=-7.65538 EndY=-5.99526 EndZ=0
    g50: LineSegment StartX=-7.65538 StartY=-5.99526 StartZ=0 EndX=-6.48644 EndY=-5.99526 EndZ=0
    g51: LineSegment StartX=-6.77343 StartY=-8 StartZ=0 EndX=-8.43343 EndY=-8 EndZ=0
    g52: LineSegment StartX=-8.43343 StartY=-8 StartZ=0 EndX=-8.43343 EndY=-10 EndZ=0
    g53: LineSegment StartX=-8.43343 StartY=-10 StartZ=0 EndX=-7.19003 EndY=-10 EndZ=0
  constraints (112):
    c: Horizontal(g0)
    c: Distance(g0) = 2
    c: Block(g0)
    c: Vertical(g1)
    c: Coincident(g2,g0)
    c: Vertical(g2)
    c: Block(g2)
    c: Coincident(g6,g2)
    c: Weight(g3) = 1
    c: Equal(g3,g4)
    c: Equal(g3,g5)
    c: InternalAlignment(g3,g6)
    c: InternalAlignment(g4,g6)
    c: InternalAlignment(g5,g6)
    c: InternalAlignment(g7,g6)
    c: InternalAlignment(g8,g6)
    c: Block(g6)
    c: Coincident(g9,g1)
    c: Coincident(g9,g6)
    c: Horizontal(g9)
    c: Vertical(g10)
    c: Block(g10)
    c: Horizontal(g11)
    c: Block(g11)
    c: Coincident(g12,g10)
    c: Horizontal(g12)
    c: Block(g12)
    c: Coincident(g13,g11)
    c: Vertical(g13)
    c: Block(g13)
    c: Coincident(g14,g10)
    c: Horizontal(g14)
    c: Block(g14)
    c: Block(g9)
    c: Block(g1)
    c: Weight(g15) = 1
    c: Equal(g15,g16)
    c: Equal(g15,g17)
    c: InternalAlignment(g15,g18)
    c: InternalAlignment(g16,g18)
    c: InternalAlignment(g17,g18)
    c: InternalAlignment(g19,g18)
    c: InternalAlignment(g20,g18)
    c: Weight(g21) = 1
    c: Equal(g21,g22)
    c: Equal(g21,g23)
    c: InternalAlignment(g21,g24)
    c: InternalAlignment(g22,g24)
    c: InternalAlignment(g23,g24)
    c: InternalAlignment(g25,g24)
    c: InternalAlignment(g26,g24)
    c: Weight(g27) = 1
    c: Equal(g27,g28)
    c: Equal(g27,g29)
    c: Coincident(g30,g14)
    c: InternalAlignment(g27,g30)
    c: InternalAlignment(g28,g30)
    c: InternalAlignment(g29,g30)
    c: InternalAlignment(g31,g30)
    c: InternalAlignment(g32,g30)
    c: Coincident(g36,g12)
    c: Weight(g33) = 1
    c: Equal(g33,g34)
    c: Equal(g33,g35)
    c: Coincident(g36,g11)
    c: InternalAlignment(g33,g36)
    c: InternalAlignment(g34,g36)
    c: InternalAlignment(g35,g36)
    c: InternalAlignment(g37,g36)
    c: InternalAlignment(g38,g36)
    c: Coincident(g42,g13)
    c: Weight(g39) = 1
    c: Equal(g39,g40)
    c: Equal(g39,g41)
    c: Coincident(g42,g1)
    c: InternalAlignment(g39,g42)
    c: InternalAlignment(g40,g42)
    c: InternalAlignment(g41,g42)
    c: InternalAlignment(g43,g42)
    c: InternalAlignment(g44,g42)
    c: Block(g18)
    c: Block(g24)
    c: Block(g30)
    c: Block(g36)
    c: Block(g42)
    c: Horizontal(g45)
    c: Coincident(g45,g0)
    c: Vertical(g46)
    c: Coincident(g46,g45)
    c: Coincident(g47,g46)
    c: Coincident(g47,g18)
    c: Horizontal(g47)
    c: Block(g46)
    c: Coincident(g48,g18)
    c: Horizontal(g48)
    c: Distance(g48) = 1.33
    c: Vertical(g49)
    c: Coincident(g49,g48)
    c: Coincident(g50,g49)
    c: Coincident(g50,g24)
    c: Horizontal(g50)
    c: Tangent(g50,g22)
    c: Horizontal(g51)
    c: Coincident(g51,g24)
    c: Block(g51)
    c: Vertical(g52)
    c: Block(g52)
    c: Coincident(g52,g51)
    c: Coincident(g53,g52)
    c: Coincident(g53,g30)
    c: Horizontal(g53)
    c: Distance(g1) = 8.5
FEATURE [Part::Feature] Face024
  shape: bbox 9.8 x 26.5 x 2e-07 mm, 1 faces, 0 solids (baked)
FEATURE [Part::Revolution] Revolve024
  Angle = 360
  Axis = (0,1,0)
  Base = (0,0,0)
  FaceMakerClass = Part::FaceMakerBullseye
  Placement = pos=(0,0,0) rot=(0,0,1;1.5708rad)
  Solid = false
  Source = -> Face024
  Symmetric = false
FEATURE [Part::Feature] Face025
  shape: bbox 9.8 x 26.5 x 2e-07 mm, 1 faces, 0 solids (baked)
FEATURE [Part::Revolution] Revolve025
  Angle = 360
  Axis = (0,1,0)
  Base = (0,0,0)
  FaceMakerClass = Part::FaceMakerBullseye
  Placement = pos=(0,0,0) rot=(0,0,1;1.5708rad)
  Solid = false
  Source = -> Face025
  Symmetric = false
FEATURE [Part::MultiFuse] Fusion033
  Placement = pos=(-18,19,36) rot=(0,0,1;0rad)
  Shapes = -> [Revolve025,Revolve024]
FEATURE [Part::Cylinder] Cylinder014
  Angle = 360
  AttacherType = Attacher::AttachEngine3D
  Height = 20
  Placement = pos=(0,0,36.15) rot=(0,0,1;0rad)
  Radius = 14.3
FEATURE [Part::Cylinder] Cylinder015
  Angle = 360
  AttacherType = Attacher::AttachEngine3D
  Height = 10
  Placement = pos=(0,0,36.15) rot=(0,0,1;0rad)
  Radius = 4
FEATURE [Part::MultiFuse] Fusion034  label="removeToCreteHoleForPlugHousing004"
  Placement = pos=(-42,19,36) rot=(0,1,0;1.5708rad)
  Shapes = -> [Cylinder014,Cylinder015]
FEATURE [Part::Cut] Cut008  label="top004"
  Base = -> Cut004
  Placement = pos=(-1,0,0) rot=(0,0,1;0rad)
  Tool = -> Fusion034
FEATURE [Part::Box] Box005  label="Cube005"
  AttacherType = Attacher::AttachEngine3D
  Height = 28
  Length = 3
  Placement = pos=(110.7,19,22) rot=(0,0,1;0rad)
  Width = 15.7
FEATURE [Part::Cylinder] Cylinder016
  Angle = 360
  AttacherType = Attacher::AttachEngine3D
  Height = 10
  Placement = pos=(0,0,36.15) rot=(0,0,1;0rad)
  Radius = 4
FEATURE [Part::Cylinder] Cylinder017
  Angle = 360
  AttacherType = Attacher::AttachEngine3D
  Height = 20
  Placement = pos=(0,0,36.15) rot=(0,0,1;0rad)
  Radius = 10.3
FEATURE [Part::MultiFuse] Fusion035  label="removeToCreteHoleForPlugHousing005"
  Placement = pos=(70,19,36) rot=(0,1,0;1.5708rad)
  Shapes = -> [Cylinder017,Cylinder016]
FEATURE [Part::Cut] Cut009  label="plugHousingTab001"
  Base = -> Box005
  Placement = pos=(-107.4,-14,0) rot=(0,0,1;0rad)
  Tool = -> Fusion035
FEATURE [Part::Box] Box006  label="Cube006"
  AttacherType = Attacher::AttachEngine3D
  Height = 28
  Length = 3
  Placement = pos=(110.7,19,22) rot=(0,0,1;0rad)
  Width = 15.7
FEATURE [Part::Cylinder] Cylinder018
  Angle = 360
  AttacherType = Attacher::AttachEngine3D
  Height = 10
  Placement = pos=(0,0,36.15) rot=(0,0,1;0rad)
  Radius = 4
FEATURE [Part::Cylinder] Cylinder019
  Angle = 360
  AttacherType = Attacher::AttachEngine3D
  Height = 20
  Placement = pos=(0,0,36.15) rot=(0,0,1;0rad)
  Radius = 10.3
FEATURE [Part::MultiFuse] Fusion036  label="removeToCreteHoleForPlugHousing006"
  Placement = pos=(70,19,36) rot=(0,1,0;1.5708rad)
  Shapes = -> [Cylinder019,Cylinder018]
FEATURE [Part::Cut] Cut010  label="plugHousingTab002"
  Base = -> Box006
  Placement = pos=(-107.4,-14,0) rot=(0,0,1;0rad)
  Tool = -> Fusion036
FEATURE [Part::MultiFuse] Fusion037
  Placement = pos=(9.6,23,0) rot=(0,0,1;3.14159rad)
  Shapes = -> [Cut009,Cut010]
FEATURE [Part::Box] Box  label="Cube"
  AttacherType = Attacher::AttachEngine3D
  Height = 10
  Length = 3
  Placement = pos=(3.3,4,12) rot=(0,0,1;0rad)
  Width = 10
FEATURE [Part::Fillet] Fillet004
  Base = -> Fusion028
  Edges = 1 edges r=2: [Edge25]
FEATURE [Part::Fillet] Fillet005  label="plugHousing046"
  Base = -> Fillet004
  Edges = 1 edges r=2: [Edge8]
FEATURE [Part::Fillet] Fillet006
  Base = -> Box
  Edges = 1 edges r=2: [Edge11]
FEATURE [Part::Box] Box007  label="Cube007"
  AttacherType = Attacher::AttachEngine3D
  Height = 10
  Length = 3
  Placement = pos=(3.3,4,50) rot=(0,0,1;0rad)
  Width = 10
FEATURE [Part::Fillet] Fillet007
  Base = -> Box007
  Edges = 1 edges r=2: [Edge12]
FEATURE [Part::Box] Box008  label="Cube008"
  AttacherType = Attacher::AttachEngine3D
  Height = 28
  Length = 4
  Placement = pos=(5,0,22) rot=(0,0,1;0rad)
  Width = 10
FEATURE [Part::Fillet] Fillet008
  Base = -> Box008
  Edges = 1 edges r=1: [Edge7]
FEATURE [Part::Fillet] Fillet009
  Base = -> Fillet008
  Edges = 1 edges r=2: [Edge5]
FEATURE [Part::Fillet] Fillet010
  Base = -> Fillet009
  Edges = 1 edges r=2: [Edge2]
FEATURE [Sketcher::SketchObject] Sketch009  label="topSketch003"
  FullyConstrained = true
  sketch-geometry (4):
    g0: LineSegment StartX=16.8446 StartY=31.512 StartZ=0 EndX=16.3251 EndY=34.4666 EndZ=0
    g1: ArcOfCircle CenterX=19 CenterY=19.2524 CenterZ=0 NormalX=0 NormalY=0 NormalZ=1 AngleXU=0 Radius=15.4476 StartAngle=1.74483 EndAngle=2.72717
    g2: ArcOfCircle CenterX=19 CenterY=19.2524 CenterZ=0 NormalX=0 NormalY=0 NormalZ=1 AngleXU=0 Radius=12.4476 StartAngle=1.74483 EndAngle=2.73189
    g3: LineSegment StartX=4.86004 StartY=25.4725 StartZ=0 EndX=7.58253 EndY=24.2107 EndZ=0
  constraints (7):
    c: Block(g0)
    c: Coincident(g1,g0)
    c: Coincident(g2,g0)
    c: Coincident(g3,g1)
    c: Coincident(g3,g2)
    c: Block(g1)
    c: Block(g2)
FEATURE [Part::Extrusion] Extrude008
  Base = -> Sketch009
  Dir = (0,0,1)
  DirMode = 2
  FaceMakerClass = Part::FaceMakerBullseye
  LengthFwd = 10
  LengthRev = 0
  Placement = pos=(0,0,31) rot=(0,0,1;0rad)
  Solid = true
  Symmetric = false
FEATURE [Part::Cylinder] Cylinder020
  Angle = 360
  AttacherType = Attacher::AttachEngine3D
  Height = 20
  Placement = pos=(0,0,36.15) rot=(0,0,1;0rad)
  Radius = 8.2
FEATURE [Part::Cylinder] Cylinder021
  Angle = 360
  AttacherType = Attacher::AttachEngine3D
  Height = 10
  Placement = pos=(0,0,36.15) rot=(0,0,1;0rad)
  Radius = 4
FEATURE [Part::MultiFuse] Fusion038  label="removeToCreteHoleForPlugHousing007"
  Placement = pos=(-42,19,36) rot=(0,1,0;1.5708rad)
  Shapes = -> [Cylinder020,Cylinder021]
FEATURE [Part::Cut] Cut011
  Base = -> Extrude008
  Tool = -> Fusion038
FEATURE [Part::Fillet] Fillet011
  Base = -> Cut011
  Edges = 1 edges r=2: [Edge1]
FEATURE [Part::Fillet] Fillet012
  Base = -> Fillet011
  Edges = 1 edges r=2.5: [Edge1]
FEATURE [Part::Fillet] Fillet013
  Base = -> Fillet012
  Edges = 1 edges r=2.5: [Edge2]
FEATURE [Part::Box] Box010  label="Cube010"
  AttacherType = Attacher::AttachEngine3D
  Height = 16
  Length = 8
  Placement = pos=(12.7,31.52,28) rot=(0,0,1;0rad)
  Width = 4
FEATURE [Sketcher::SketchObject] Sketch010  label="topSketch004"
  FullyConstrained = true
  sketch-geometry (4):
    g0: LineSegment StartX=16.8446 StartY=31.512 StartZ=0 EndX=16.3251 EndY=34.4666 EndZ=0
    g1: ArcOfCircle CenterX=19 CenterY=19.2524 CenterZ=0 NormalX=0 NormalY=0 NormalZ=1 AngleXU=0 Radius=15.4476 StartAngle=1.74483 EndAngle=2.72717
    g2: ArcOfCircle CenterX=19 CenterY=19.2524 CenterZ=0 NormalX=0 NormalY=0 NormalZ=1 AngleXU=0 Radius=12.4476 StartAngle=1.74483 EndAngle=2.73189
    g3: LineSegment StartX=4.86004 StartY=25.4725 StartZ=0 EndX=7.58253 EndY=24.2107 EndZ=0
  constraints (7):
    c: Block(g0)
    c: Coincident(g1,g0)
    c: Coincident(g2,g0)
    c: Coincident(g3,g1)
    c: Coincident(g3,g2)
    c: Block(g1)
    c: Block(g2)
FEATURE [Part::Cylinder] Cylinder022
  Angle = 360
  AttacherType = Attacher::AttachEngine3D
  Height = 10
  Placement = pos=(0,0,36.15) rot=(0,0,1;0rad)
  Radius = 4
FEATURE [Sketcher::SketchObject] Sketch011  label="topSketch005"
  FullyConstrained = true
  sketch-geometry (4):
    g0: LineSegment StartX=16.8446 StartY=31.512 StartZ=0 EndX=16.3251 EndY=34.4666 EndZ=0
    g1: ArcOfCircle CenterX=19 CenterY=19.2524 CenterZ=0 NormalX=0 NormalY=0 NormalZ=1 AngleXU=0 Radius=15.4476 StartAngle=1.74483 EndAngle=2.72717
    g2: ArcOfCircle CenterX=19 CenterY=19.2524 CenterZ=0 NormalX=0 NormalY=0 NormalZ=1 AngleXU=0 Radius=12.4476 StartAngle=1.74483 EndAngle=2.73189
    g3: LineSegment StartX=4.86004 StartY=25.4725 StartZ=0 EndX=7.58253 EndY=24.2107 EndZ=0
  constraints (7):
    c: Block(g0)
    c: Coincident(g1,g0)
    c: Coincident(g2,g0)
    c: Coincident(g3,g1)
    c: Coincident(g3,g2)
    c: Block(g1)
    c: Block(g2)
FEATURE [Part::Extrusion] Extrude010
  Base = -> Sketch011
  Dir = (0,0,1)
  DirMode = 2
  FaceMakerClass = Part::FaceMakerBullseye
  LengthFwd = 10.6
  LengthRev = 0
  Placement = pos=(0,0,31) rot=(0,0,1;0rad)
  Solid = true
  Symmetric = false
FEATURE [Part::Cylinder] Cylinder023
  Angle = 360
  AttacherType = Attacher::AttachEngine3D
  Height = 20
  Placement = pos=(0,0,36.15) rot=(0,0,1;0rad)
  Radius = 8.2
FEATURE [Part::MultiFuse] Fusion039  label="removeToCreteHoleForPlugHousing008"
  Placement = pos=(-42,19,36) rot=(0,1,0;1.5708rad)
  Shapes = -> [Cylinder023,Cylinder022]
FEATURE [Part::Cut] Cut012
  Base = -> Extrude010
  Placement = pos=(0,0,-0.3) rot=(0,0,1;0rad)
  Tool = -> Fusion039
FEATURE [Part::Cut] Cut013
  Base = -> Box010
  Tool = -> Cut012
FEATURE [Part::Fillet] Fillet014
  Base = -> Cut013
  Edges = 1 edges r=0.7: [Edge13]
FEATURE [Part::Fillet] Fillet015
  Base = -> Fillet014
  Edges = 1 edges r=0.7: [Edge13]
FEATURE [Part::Fillet] Fillet016
  Base = -> Fillet015
  Edges = 1 edges r=0.7: [Edge16]
FEATURE [Part::Fillet] Fillet017
  Base = -> Fillet016
  Edges = 1 edges r=0.7: [Edge11]
FEATURE [Part::Fillet] Fillet018
  Base = -> Fillet017
  Edges = 1 edges r=0.7: [Edge10]
FEATURE [Part::Fillet] Fillet019
  Base = -> Fillet018
  Edges = 1 edges r=1.2: [Edge5]
FEATURE [Part::Fillet] Fillet020
  Base = -> Fillet019
  Edges = 1 edges r=1.2: [Edge12]
FEATURE [Part::Fillet] Fillet021
  Base = -> Fillet020
  Edges = 1 edges r=2: [Edge1]
  Placement = pos=(0.3,0,0) rot=(0,0,1;0rad)
FEATURE [Part::MultiFuse] Fusion040  label="top005"
  Shapes = -> [Cut008,Fillet021]
FEATURE [Part::MultiFuse] Fusion041  label="wireHolder"
  Shapes = -> [Fusion033,Fillet013]
FEATURE [Part::MultiFuse] Fusion042
  Shapes = -> [Fillet007,Fusion041]
FEATURE [Part::MultiFuse] Fusion043  label="wireHolder001"
  Shapes = -> [Fusion042,Fillet010]
FEATURE [Part::MultiFuse] Fusion044  label="wireHolder002"
  Shapes = -> [Fillet006,Fusion037,Fusion043]
FEATURE [Part::Feature] Face026
  shape: bbox 11 x 6 x 2e-07 mm, 1 faces, 0 solids (baked)
FEATURE [Part::Revolution] Revolve026
  Angle = 360
  Axis = (0,1,0)
  Base = (0,0,0)
  FaceMakerClass = Part::FaceMakerBullseye
  Placement = pos=(30.3,-1,19.7) rot=(0,0,1;0rad)
  Solid = false
  Source = -> Face026
  Symmetric = false
FEATURE [Sketcher::SketchObject] Sketch013  label="topSketch006"
  FullyConstrained = true
  sketch-geometry (13):
    g0: LineSegment StartX=117 StartY=19 StartZ=0 EndX=117 EndY=38 EndZ=0
    g1: ArcOfCircle CenterX=98 CenterY=19 CenterZ=0 NormalX=0 NormalY=0 NormalZ=1 AngleXU=0 Radius=19 StartAngle=5.7297 EndAngle=6.28319
    g2: LineSegment StartX=0 StartY=3 StartZ=0 EndX=0 EndY=19 EndZ=0
    g3: LineSegment StartX=19 StartY=38 StartZ=0 EndX=117 EndY=38 EndZ=0
    g4: ArcOfCircle CenterX=19 CenterY=19 CenterZ=0 NormalX=0 NormalY=0 NormalZ=1 AngleXU=0 Radius=19 StartAngle=1.5708 EndAngle=3.14159
    g5: ArcOfCircle CenterX=19 CenterY=19 CenterZ=0 NormalX=0 NormalY=0 NormalZ=1 AngleXU=0 Radius=16 StartAngle=1.5708 EndAngle=3.14159
    g6: ArcOfCircle CenterX=98 CenterY=19 CenterZ=0 NormalX=0 NormalY=0 NormalZ=1 AngleXU=0 Radius=16 StartAngle=5.60905 EndAngle=6.28319
    g7: LineSegment StartX=114 StartY=19 StartZ=0 EndX=114 EndY=35 EndZ=0
    g8: LineSegment StartX=110.5 StartY=9.01251 StartZ=0 EndX=114.163 EndY=9.01251 EndZ=0
    g9: LineSegment StartX=114 StartY=35 StartZ=0 EndX=19 EndY=35 EndZ=0
    g10: LineSegment StartX=0 StartY=3 StartZ=0 EndX=0 EndY=0 EndZ=0
    g11: LineSegment StartX=3 StartY=0 StartZ=0 EndX=0 EndY=0 EndZ=0
    g12: LineSegment StartX=3 StartY=19 StartZ=0 EndX=3 EndY=0 EndZ=0
  constraints (33):
    c: Vertical(g0)
    c: Distance(g0) = 19
    c: Block(g0)
    c: Coincident(g1,g0)
    c: Block(g1)
    c: Vertical(g2)
    c: Block(g2)
    c: Coincident(g3,g0)
    c: Horizontal(g3)
    c: Distance(g3) = 98
    c: Coincident(g4,g3)
    c: Coincident(g4,g2)
    c: Block(g4)
    c: Coincident(g5,g4)
    c: Coincident(g6,g1)
    c: Block(g6)
    c: Block(g5)
    c: Coincident(g7,g6)
    c: Vertical(g7)
    c: Coincident(g8,g6)
    c: Coincident(g8,g1)
    c: Coincident(g9,g7)
    c: Coincident(g9,g5)
    c: Horizontal(g9)
    c: Tangent(g9,g5)
    c: Coincident(g10,g2)
    c: Distance(g10) = 3
    c: Vertical(g10)
    c: Coincident(g11,g10)
    c: Horizontal(g11)
    c: Coincident(g12,g5)
    c: Coincident(g12,g11)
    c: Vertical(g12)
FEATURE [Part::Extrusion] Extrude011  label="top006"
  Base = -> Sketch013
  Dir = (0,0,1)
  DirMode = 2
  FaceMakerClass = Part::FaceMakerBullseye
  LengthFwd = 72
  LengthRev = 0
  Solid = true
  Symmetric = false
FEATURE [Sketcher::SketchObject] Sketch014
  FullyConstrained = true
  MapMode = 3
  Placement = pos=(0,0,0) rot=(1,0,0;1.5708rad)
  Support = -> [Extrude011]
  sketch-geometry (8):
    g0: Circle CenterX=80.351 CenterY=-67.6202 CenterZ=0 NormalX=0 NormalY=0 NormalZ=1 AngleXU=0 Radius=2
    g1: Circle CenterX=80.351 CenterY=-67.6202 CenterZ=0 NormalX=0 NormalY=0 NormalZ=1 AngleXU=0 Radius=3
    g2: Circle CenterX=80.351 CenterY=-4.92017 CenterZ=0 NormalX=0 NormalY=0 NormalZ=1 AngleXU=0 Radius=2
    g3: Circle CenterX=80.351 CenterY=-4.92017 CenterZ=0 NormalX=0 NormalY=0 NormalZ=1 AngleXU=0 Radius=3
    g4: Circle CenterX=23.851 CenterY=-4.92017 CenterZ=0 NormalX=0 NormalY=0 NormalZ=1 AngleXU=0 Radius=2
    g5: Circle CenterX=23.851 CenterY=-4.92017 CenterZ=0 NormalX=0 NormalY=0 NormalZ=1 AngleXU=0 Radius=3
    g6: Circle CenterX=23.851 CenterY=-67.6202 CenterZ=0 NormalX=0 NormalY=0 NormalZ=1 AngleXU=0 Radius=2
    g7: Circle CenterX=23.851 CenterY=-67.6202 CenterZ=0 NormalX=0 NormalY=0 NormalZ=1 AngleXU=0 Radius=3
  constraints (8):
    c: Block(g3)
    c: Block(g2)
    c: Block(g1)
    c: Block(g0)
    c: Block(g6)
    c: Block(g7)
    c: Block(g4)
    c: Block(g5)
FEATURE [Part::Feature] Face027
  shape: bbox 11 x 6 x 2e-07 mm, 1 faces, 0 solids (baked)
FEATURE [Part::Revolution] Revolve027
  Angle = 360
  Axis = (0,1,0)
  Base = (0,0,0)
  FaceMakerClass = Part::FaceMakerBullseye
  Placement = pos=(30.3,-1,51.7) rot=(0,0,1;0rad)
  Solid = false
  Source = -> Face027
  Symmetric = false
FEATURE [Part::Feature] Face028
  shape: bbox 11 x 6 x 2e-07 mm, 1 faces, 0 solids (baked)
FEATURE [Part::Revolution] Revolve028
  Angle = 360
  Axis = (0,1,0)
  Base = (0,0,0)
  FaceMakerClass = Part::FaceMakerBullseye
  Placement = pos=(62.3,-1,19.7) rot=(0,0,1;0rad)
  Solid = false
  Source = -> Face028
  Symmetric = false
FEATURE [Part::Feature] Face029
  shape: bbox 11 x 6 x 2e-07 mm, 1 faces, 0 solids (baked)
FEATURE [Part::Revolution] Revolve029
  Angle = 360
  Axis = (0,1,0)
  Base = (0,0,0)
  FaceMakerClass = Part::FaceMakerBullseye
  Placement = pos=(62.3,-1,51.7) rot=(0,0,1;0rad)
  Solid = false
  Source = -> Face029
  Symmetric = false
FEATURE [Part::Feature] Wire
  shape: bbox 11 x 5.2 x 2e-07 mm, 0 faces, 0 solids (baked)
FEATURE [Part::Revolution] Revolve030
  Angle = 360
  Axis = (0,1,0)
  Base = (0,0,0)
  FaceMakerClass = Part::FaceMakerBullseye
  Placement = pos=(30.3,38,19.7) rot=(0,0,1;0rad)
  Solid = true
  Source = -> Wire
  Symmetric = false
FEATURE [Part::Feature] Wire001
  shape: bbox 11 x 5.2 x 2e-07 mm, 0 faces, 0 solids (baked)
FEATURE [Part::Revolution] Revolve031
  Angle = 360
  Axis = (0,1,0)
  Base = (0,0,0)
  FaceMakerClass = Part::FaceMakerBullseye
  Placement = pos=(30.3,38,51.7) rot=(0,0,1;0rad)
  Solid = true
  Source = -> Wire001
  Symmetric = false
FEATURE [Part::Feature] Wire002
  shape: bbox 11 x 5.2 x 2e-07 mm, 0 faces, 0 solids (baked)
FEATURE [Part::Revolution] Revolve032
  Angle = 360
  Axis = (0,1,0)
  Base = (0,0,0)
  FaceMakerClass = Part::FaceMakerBullseye
  Placement = pos=(62.3,38,51.7) rot=(0,0,1;0rad)
  Solid = true
  Source = -> Wire002
  Symmetric = false
FEATURE [Part::Feature] Wire003
  shape: bbox 11 x 5.2 x 2e-07 mm, 0 faces, 0 solids (baked)
FEATURE [Part::Revolution] Revolve033
  Angle = 360
  Axis = (0,1,0)
  Base = (0,0,0)
  FaceMakerClass = Part::FaceMakerBullseye
  Placement = pos=(62.3,38,19.7) rot=(0,0,1;0rad)
  Solid = true
  Source = -> Wire003
  Symmetric = false
FEATURE [Part::MultiFuse] Fusion045  label="altRandScrewHousing"
  Shapes = -> [Revolve029,Revolve027,Revolve028,Revolve026]
FEATURE [Part::MultiFuse] Fusion046  label="fanScrewHousing"
  Shapes = -> [Revolve033,Revolve032,Revolve031,Revolve030]
FEATURE [Sketcher::SketchObject] Sketch015
  FullyConstrained = true
  sketch-geometry (17):
    g0: Circle CenterX=-3.5 CenterY=23.5 CenterZ=0 NormalX=0 NormalY=0 NormalZ=1 AngleXU=0 Radius=1
    g1: Circle CenterX=-1 CenterY=15.25 CenterZ=0 NormalX=0 NormalY=0 NormalZ=1 AngleXU=0 Radius=1
    g2: Circle CenterX=-3.5 CenterY=7 CenterZ=0 NormalX=0 NormalY=0 NormalZ=1 AngleXU=0 Radius=1
    g3: BSplineCurve PolesCount=3 KnotsCount=2 Degree=2 IsPeriodic=0
    g4: GeomPoint X=-3.5 Y=23.5 Z=0
    g5: GeomPoint X=-3.5 Y=7 Z=0
    g6: Circle CenterX=-4.8 CenterY=30.5 CenterZ=0 NormalX=0 NormalY=0 NormalZ=1 AngleXU=0 Radius=1
    g7: Circle CenterX=-3.5 CenterY=30.5 CenterZ=0 NormalX=0 NormalY=0 NormalZ=1 AngleXU=0 Radius=1
    g8: Circle CenterX=-3.5 CenterY=29.2 CenterZ=0 NormalX=0 NormalY=0 NormalZ=1 AngleXU=0 Radius=1
    g9: BSplineCurve PolesCount=3 KnotsCount=2 Degree=2 IsPeriodic=0
    g10: GeomPoint X=-4.8 Y=30.5 Z=0
    g11: GeomPoint X=-3.5 Y=29.2 Z=0
    g12: LineSegment StartX=-3.5 StartY=29.2 StartZ=0 EndX=-3.5 EndY=23.5 EndZ=0
    g13: LineSegment StartX=-4.8 StartY=30.5 StartZ=0 EndX=0 EndY=30.5 EndZ=0
    g14: LineSegment StartX=-3.5 StartY=0.3 StartZ=0 EndX=0 EndY=0.3 EndZ=0
    g15: LineSegment StartX=-3.5 StartY=0.3 StartZ=0 EndX=-3.5 EndY=7 EndZ=0
    g16: LineSegment StartX=0 StartY=0.3 StartZ=0 EndX=0 EndY=30.5 EndZ=0
  constraints (33):
    c: Weight(g0) = 1
    c: Equal(g0,g1)
    c: Equal(g0,g2)
    c: InternalAlignment(g0,g3)
    c: InternalAlignment(g1,g3)
    c: InternalAlignment(g2,g3)
    c: InternalAlignment(g4,g3)
    c: InternalAlignment(g5,g3)
    c: Block(g3)
    c: Weight(g6) = 1
    c: Equal(g6,g7)
    c: Equal(g6,g8)
    c: InternalAlignment(g6,g9)
    c: InternalAlignment(g7,g9)
    c: InternalAlignment(g8,g9)
    c: InternalAlignment(g10,g9)
    c: InternalAlignment(g11,g9)
    c: Block(g9)
    c: Coincident(g12,g9)
    c: Coincident(g12,g3)
    c: Vertical(g12)
    c: Coincident(g13,g9)
    c: Horizontal(g13)
    c: Distance(g13) = 4.8
    c: Horizontal(g14)
    c: Block(g14)
    c: Coincident(g15,g14)
    c: Coincident(g15,g3)
    c: Vertical(g15)
    c: Coincident(g16,g14)
    c: Coincident(g16,g13)
    c: Vertical(g16)
    c: Tangent(g16,g1)
FEATURE [Sketcher::SketchObject] Sketch016
  FullyConstrained = true
  sketch-geometry (16):
    g0: Circle CenterX=-3.5 CenterY=23.5 CenterZ=0 NormalX=0 NormalY=0 NormalZ=1 AngleXU=0 Radius=1
    g1: Circle CenterX=-1 CenterY=15.25 CenterZ=0 NormalX=0 NormalY=0 NormalZ=1 AngleXU=0 Radius=1
    g2: Circle CenterX=-3.5 CenterY=7 CenterZ=0 NormalX=0 NormalY=0 NormalZ=1 AngleXU=0 Radius=1
    g3: BSplineCurve PolesCount=3 KnotsCount=2 Degree=2 IsPeriodic=0
    g4: GeomPoint X=-3.5 Y=23.5 Z=0
    g5: GeomPoint X=-3.5 Y=7 Z=0
    g6: LineSegment StartX=-3.5 StartY=28.2 StartZ=0 EndX=-3.5 EndY=23.5 EndZ=0
    g7: LineSegment StartX=0 StartY=29.5 StartZ=0 EndX=0 EndY=30 EndZ=0
    g8: LineSegment StartX=-3.5 StartY=28.2 StartZ=0 EndX=-3.5 EndY=30 EndZ=0
    g9: LineSegment StartX=0 StartY=30 StartZ=0 EndX=0 EndY=30.5 EndZ=0
    g10: LineSegment StartX=0 StartY=30.5 StartZ=0 EndX=-3.5 EndY=30.5 EndZ=0
    g11: LineSegment StartX=-3.5 StartY=30.5 StartZ=0 EndX=-3.5 EndY=30 EndZ=0
    g12: LineSegment StartX=0 StartY=29.5 StartZ=0 EndX=0 EndY=5 EndZ=0
    g13: LineSegment StartX=-3.5 StartY=0.3 StartZ=0 EndX=-3.5 EndY=7 EndZ=0
    g14: LineSegment StartX=-3.5 StartY=0.3 StartZ=0 EndX=0 EndY=0.3 EndZ=0
    g15: LineSegment StartX=0 StartY=5 StartZ=0 EndX=0 EndY=0.3 EndZ=0
  constraints (39):
    c: Weight(g0) = 1
    c: Equal(g0,g1)
    c: Equal(g0,g2)
    c: InternalAlignment(g0,g3)
    c: InternalAlignment(g1,g3)
    c: InternalAlignment(g2,g3)
    c: InternalAlignment(g4,g3)
    c: InternalAlignment(g5,g3)
    c: Block(g3)
    c: Coincident(g6,g3)
    c: Vertical(g6)
    c: Vertical(g7)
    c: Distance(g7) = 0.5
    c: Coincident(g8,g6)
    c: Vertical(g8)
    c: Block(g6)
    c: Block(g7)
    c: Vertical(g9)
    c: Equal(g7,g9) = 0.5
    c: Block(g9)
    c: Coincident(g9,g7)
    c: Horizontal(g10)
    c: Coincident(g10,g9)
    c: Coincident(g11,g10)
    c: Coincident(g11,g8)
    c: Vertical(g11)
    c: Block(g11)
    c: Coincident(g12,g7)
    c: Vertical(g12)
    c: Coincident(g13,g3)
    c: Vertical(g13)
    c: Distance(g13) = 6.7
    c: Coincident(g14,g13)
    c: Horizontal(g14)
    c: Block(g14)
    c: Coincident(g15,g12)
    c: Coincident(g15,g14)
    c: Vertical(g15)
    c: Block(g15)
FEATURE [Sketcher::SketchObject] Sketch017
  FullyConstrained = true
  sketch-geometry (11):
    g0: LineSegment StartX=-3.5 StartY=1e-16 StartZ=0 EndX=-1.6 EndY=1e-16 EndZ=0
    g1: LineSegment StartX=-1.6 StartY=1e-16 StartZ=0 EndX=-1.6 EndY=1.5 EndZ=0
    g2: LineSegment StartX=-3.5 StartY=1.5 StartZ=0 EndX=-1.6 EndY=1.5 EndZ=0
    g3: LineSegment StartX=-3.5 StartY=1e-16 StartZ=0 EndX=-4.8 EndY=1e-16 EndZ=0
    g4: Circle CenterX=-3.5 CenterY=1.3 CenterZ=0 NormalX=0 NormalY=0 NormalZ=1 AngleXU=0 Radius=1
    g5: Circle CenterX=-3.5 CenterY=1e-16 CenterZ=0 NormalX=0 NormalY=0 NormalZ=1 AngleXU=0 Radius=1
    g6: Circle CenterX=-4.8 CenterY=1e-16 CenterZ=0 NormalX=0 NormalY=0 NormalZ=1 AngleXU=0 Radius=1
    g7: BSplineCurve PolesCount=3 KnotsCount=2 Degree=2 IsPeriodic=0
    g8: GeomPoint X=-3.5 Y=1.3 Z=0
    g9: GeomPoint X=-4.8 Y=1e-16 Z=0
    g10: LineSegment StartX=-3.5 StartY=1.3 StartZ=0 EndX=-3.5 EndY=1.5 EndZ=0
  constraints (24):
    c: Horizontal(g0)
    c: Distance(g0) = 1.9
    c: Block(g0)
    c: Coincident(g1,g0)
    c: Vertical(g1)
    c: Coincident(g2,g1)
    c: Horizontal(g2)
    c: Coincident(g3,g0)
    c: Horizontal(g3)
    c: Distance(g3) = 1.3
    c: Weight(g4) = 1
    c: Equal(g4,g5)
    c: Coincident(g5,g0)
    c: Equal(g4,g6)
    c: Coincident(g7,g3)
    c: InternalAlignment(g4,g7)
    c: InternalAlignment(g5,g7)
    c: InternalAlignment(g6,g7)
    c: InternalAlignment(g8,g7)
    c: InternalAlignment(g9,g7)
    c: Coincident(g10,g7)
    c: Coincident(g10,g2)
    c: Vertical(g10)
    c: Block(g10)
FEATURE [Part::Feature] Face035
  shape: bbox 3.2 x 1.5 x 2e-07 mm, 1 faces, 0 solids (baked)
FEATURE [Part::Revolution] Revolve039  label="backCaseScrewRetainer"
  Angle = 360
  Axis = (0,1,0)
  Base = (0,0,0)
  FaceMakerClass = Part::FaceMakerBullseye
  Placement = pos=(12.5,3,62) rot=(0,0,1;0rad)
  Solid = false
  Source = -> Face035
  Symmetric = false
FEATURE [Part::Feature] Face036
  shape: bbox 3.2 x 1.5 x 2e-07 mm, 1 faces, 0 solids (baked)
FEATURE [Part::Feature] Face039
  shape: bbox 4.8 x 30.2 x 2e-07 mm, 1 faces, 0 solids (baked)
FEATURE [Part::Revolution] Revolve043  label="frontCaseScrewPost002"
  Angle = 360
  Axis = (0,1,0)
  Base = (0,0,0)
  FaceMakerClass = Part::FaceMakerBullseye
  Placement = pos=(89.5,4.5,3.5) rot=(0,0,1;0rad)
  Solid = false
  Source = -> Face039
  Symmetric = false
FEATURE [Part::Feature] Face042
  shape: bbox 4.8 x 30.2 x 2e-07 mm, 1 faces, 0 solids (baked)
FEATURE [Part::Revolution] Revolve046  label="frontCaseScrewPost003"
  Angle = 360
  Axis = (0,1,0)
  Base = (0,0,0)
  FaceMakerClass = Part::FaceMakerBullseye
  Placement = pos=(89.5,4.5,68.5) rot=(0,0,1;0rad)
  Solid = false
  Source = -> Face042
  Symmetric = false
FEATURE [Part::Feature] Face043
  shape: bbox 3.2 x 1.5 x 2e-07 mm, 1 faces, 0 solids (baked)
FEATURE [Part::Revolution] Revolve047  label="frontCaseScrewRetainer002"
  Angle = 360
  Axis = (0,1,0)
  Base = (0,0,0)
  FaceMakerClass = Part::FaceMakerBullseye
  Placement = pos=(89.5,3,68.5) rot=(0,0,1;0rad)
  Solid = false
  Source = -> Face043
  Symmetric = false
FEATURE [Part::Feature] Face044
  shape: bbox 3.2 x 1.5 x 2e-07 mm, 1 faces, 0 solids (baked)
FEATURE [Part::Revolution] Revolve048  label="frontCaseScrewRetainer003"
  Angle = 360
  Axis = (0,1,0)
  Base = (0,0,0)
  FaceMakerClass = Part::FaceMakerBullseye
  Placement = pos=(89.5,3,3.5) rot=(0,0,1;0rad)
  Solid = false
  Source = -> Face044
  Symmetric = false
FEATURE [App::MeasureDistance] Distance002  label="Distance: 1.67 mm"
  Distance = 1.66921
  P1 = (99.2361,4.7524,71.7)
  P2 = (99.2347,6.42161,71.7)
FEATURE [Sketcher::SketchObject] Sketch018
  FullyConstrained = true
  sketch-geometry (7):
    g0: LineSegment StartX=0 StartY=0 StartZ=0 EndX=0 EndY=6 EndZ=0
    g1: Circle CenterX=0 CenterY=0 CenterZ=0 NormalX=0 NormalY=0 NormalZ=1 AngleXU=0 Radius=1
    g2: Circle CenterX=8 CenterY=6 CenterZ=0 NormalX=0 NormalY=0 NormalZ=1 AngleXU=0 Radius=1
    g3: BSplineCurve PolesCount=3 KnotsCount=2 Degree=2 IsPeriodic=0
    g4: GeomPoint X=0 Y=0 Z=0
    g5: GeomPoint X=8 Y=6 Z=0
    g6: LineSegment StartX=0 StartY=6 StartZ=0 EndX=8 EndY=6 EndZ=0
  constraints (14):
    c: Coincident(g0,g-1)
    c: Distance(g0) = 6
    c: Vertical(g0)
    c: Coincident(g3,g0)
    c: Weight(g1) = 1
    c: Equal(g1,g2)
    c: InternalAlignment(g1,g3)
    c: InternalAlignment(g2,g3)
    c: InternalAlignment(g4,g3)
    c: InternalAlignment(g5,g3)
    c: Block(g3)
    c: Coincident(g6,g0)
    c: Coincident(g6,g3)
    c: Horizontal(g6)
FEATURE [Part::Extrusion] Extrude012  label="caseScrewPillarBracket"
  Base = -> Sketch018
  Dir = (0,0,1)
  DirMode = 2
  FaceMakerClass = Part::FaceMakerBullseye
  LengthFwd = 2.4
  LengthRev = 0
  Placement = pos=(15.76,29,8.8) rot=(0,1,0;0rad)
  Solid = true
  Symmetric = false
FEATURE [Sketcher::SketchObject] Sketch019
  FullyConstrained = true
  sketch-geometry (7):
    g0: LineSegment StartX=0 StartY=0 StartZ=0 EndX=0 EndY=6 EndZ=0
    g1: Circle CenterX=0 CenterY=0 CenterZ=0 NormalX=0 NormalY=0 NormalZ=1 AngleXU=0 Radius=1
    g2: Circle CenterX=8 CenterY=6 CenterZ=0 NormalX=0 NormalY=0 NormalZ=1 AngleXU=0 Radius=1
    g3: BSplineCurve PolesCount=3 KnotsCount=2 Degree=2 IsPeriodic=0
    g4: GeomPoint X=0 Y=0 Z=0
    g5: GeomPoint X=8 Y=6 Z=0
    g6: LineSegment StartX=0 StartY=6 StartZ=0 EndX=8 EndY=6 EndZ=0
  constraints (14):
    c: Coincident(g0,g-1)
    c: Distance(g0) = 6
    c: Vertical(g0)
    c: Coincident(g3,g0)
    c: Weight(g1) = 1
    c: Equal(g1,g2)
    c: InternalAlignment(g1,g3)
    c: InternalAlignment(g2,g3)
    c: InternalAlignment(g4,g3)
    c: InternalAlignment(g5,g3)
    c: Block(g3)
    c: Coincident(g6,g0)
    c: Coincident(g6,g3)
    c: Horizontal(g6)
FEATURE [Part::Extrusion] Extrude013  label="caseScrewPillarBracket001"
  Base = -> Sketch019
  Dir = (0,0,1)
  DirMode = 2
  FaceMakerClass = Part::FaceMakerBullseye
  LengthFwd = 2.4
  LengthRev = 0
  Placement = pos=(15.76,29,60.8) rot=(0,0,1;0rad)
  Solid = true
  Symmetric = false
FEATURE [Sketcher::SketchObject] Sketch020
  FullyConstrained = true
  sketch-geometry (7):
    g0: LineSegment StartX=0 StartY=0 StartZ=0 EndX=0 EndY=6 EndZ=0
    g1: Circle CenterX=0 CenterY=0 CenterZ=0 NormalX=0 NormalY=0 NormalZ=1 AngleXU=0 Radius=1
    g2: Circle CenterX=8 CenterY=6 CenterZ=0 NormalX=0 NormalY=0 NormalZ=1 AngleXU=0 Radius=1
    g3: BSplineCurve PolesCount=3 KnotsCount=2 Degree=2 IsPeriodic=0
    g4: GeomPoint X=0 Y=0 Z=0
    g5: GeomPoint X=8 Y=6 Z=0
    g6: LineSegment StartX=0 StartY=6 StartZ=0 EndX=8 EndY=6 EndZ=0
  constraints (14):
    c: Coincident(g0,g-1)
    c: Distance(g0) = 6
    c: Vertical(g0)
    c: Coincident(g3,g0)
    c: Weight(g1) = 1
    c: Equal(g1,g2)
    c: InternalAlignment(g1,g3)
    c: InternalAlignment(g2,g3)
    c: InternalAlignment(g4,g3)
    c: InternalAlignment(g5,g3)
    c: Block(g3)
    c: Coincident(g6,g0)
    c: Coincident(g6,g3)
    c: Horizontal(g6)
FEATURE [Part::Extrusion] Extrude014  label="caseScrewPillarBracket002"
  Base = -> Sketch020
  Dir = (0,0,1)
  DirMode = 2
  FaceMakerClass = Part::FaceMakerBullseye
  LengthFwd = 2.4
  LengthRev = 0
  Placement = pos=(13.7,29,13.26) rot=(0,1,0;-1.5708rad)
  Solid = true
  Symmetric = false
FEATURE [Sketcher::SketchObject] Sketch021
  FullyConstrained = true
  sketch-geometry (7):
    g0: LineSegment StartX=0 StartY=0 StartZ=0 EndX=0 EndY=6 EndZ=0
    g1: Circle CenterX=0 CenterY=0 CenterZ=0 NormalX=0 NormalY=0 NormalZ=1 AngleXU=0 Radius=1
    g2: Circle CenterX=8 CenterY=6 CenterZ=0 NormalX=0 NormalY=0 NormalZ=1 AngleXU=0 Radius=1
    g3: BSplineCurve PolesCount=3 KnotsCount=2 Degree=2 IsPeriodic=0
    g4: GeomPoint X=0 Y=0 Z=0
    g5: GeomPoint X=8 Y=6 Z=0
    g6: LineSegment StartX=0 StartY=6 StartZ=0 EndX=8 EndY=6 EndZ=0
  constraints (14):
    c: Coincident(g0,g-1)
    c: Distance(g0) = 6
    c: Vertical(g0)
    c: Coincident(g3,g0)
    c: Weight(g1) = 1
    c: Equal(g1,g2)
    c: InternalAlignment(g1,g3)
    c: InternalAlignment(g2,g3)
    c: InternalAlignment(g4,g3)
    c: InternalAlignment(g5,g3)
    c: Block(g3)
    c: Coincident(g6,g0)
    c: Coincident(g6,g3)
    c: Horizontal(g6)
FEATURE [Part::Extrusion] Extrude015  label="caseScrewPillarBracket003"
  Base = -> Sketch021
  Dir = (0,0,1)
  DirMode = 2
  FaceMakerClass = Part::FaceMakerBullseye
  LengthFwd = 2.4
  LengthRev = 0
  Placement = pos=(11.3,29,58.74) rot=(0,1,0;1.5708rad)
  Solid = true
  Symmetric = false
FEATURE [Sketcher::SketchObject] Sketch022
  FullyConstrained = true
  sketch-geometry (7):
    g0: LineSegment StartX=0 StartY=0 StartZ=0 EndX=0 EndY=6 EndZ=0
    g1: Circle CenterX=0 CenterY=0 CenterZ=0 NormalX=0 NormalY=0 NormalZ=1 AngleXU=0 Radius=1
    g2: Circle CenterX=8 CenterY=6 CenterZ=0 NormalX=0 NormalY=0 NormalZ=1 AngleXU=0 Radius=1
    g3: BSplineCurve PolesCount=3 KnotsCount=2 Degree=2 IsPeriodic=0
    g4: GeomPoint X=0 Y=0 Z=0
    g5: GeomPoint X=8 Y=6 Z=0
    g6: LineSegment StartX=0 StartY=6 StartZ=0 EndX=8 EndY=6 EndZ=0
  constraints (14):
    c: Coincident(g0,g-1)
    c: Distance(g0) = 6
    c: Vertical(g0)
    c: Coincident(g3,g0)
    c: Weight(g1) = 1
    c: Equal(g1,g2)
    c: InternalAlignment(g1,g3)
    c: InternalAlignment(g2,g3)
    c: InternalAlignment(g4,g3)
    c: InternalAlignment(g5,g3)
    c: Block(g3)
    c: Coincident(g6,g0)
    c: Coincident(g6,g3)
    c: Horizontal(g6)
FEATURE [Part::Extrusion] Extrude016  label="caseScrewPillarBracket004"
  Base = -> Sketch022
  Dir = (0,0,1)
  DirMode = 2
  FaceMakerClass = Part::FaceMakerBullseye
  LengthFwd = 2.4
  LengthRev = 0
  Placement = pos=(88.3,29,65.23) rot=(0,1,0;1.5708rad)
  Solid = true
  Symmetric = false
FEATURE [Sketcher::SketchObject] Sketch023
  FullyConstrained = true
  sketch-geometry (7):
    g0: LineSegment StartX=0 StartY=0 StartZ=0 EndX=0 EndY=6 EndZ=0
    g1: Circle CenterX=0 CenterY=0 CenterZ=0 NormalX=0 NormalY=0 NormalZ=1 AngleXU=0 Radius=1
    g2: Circle CenterX=8 CenterY=6 CenterZ=0 NormalX=0 NormalY=0 NormalZ=1 AngleXU=0 Radius=1
    g3: BSplineCurve PolesCount=3 KnotsCount=2 Degree=2 IsPeriodic=0
    g4: GeomPoint X=0 Y=0 Z=0
    g5: GeomPoint X=8 Y=6 Z=0
    g6: LineSegment StartX=0 StartY=6 StartZ=0 EndX=8 EndY=6 EndZ=0
  constraints (14):
    c: Coincident(g0,g-1)
    c: Distance(g0) = 6
    c: Vertical(g0)
    c: Coincident(g3,g0)
    c: Weight(g1) = 1
    c: Equal(g1,g2)
    c: InternalAlignment(g1,g3)
    c: InternalAlignment(g2,g3)
    c: InternalAlignment(g4,g3)
    c: InternalAlignment(g5,g3)
    c: Block(g3)
    c: Coincident(g6,g0)
    c: Coincident(g6,g3)
    c: Horizontal(g6)
FEATURE [Part::Extrusion] Extrude017  label="caseScrewPillarBracket005"
  Base = -> Sketch023
  Dir = (0,0,1)
  DirMode = 2
  FaceMakerClass = Part::FaceMakerBullseye
  LengthFwd = 2.4
  LengthRev = 0
  Placement = pos=(90.7,29,6.77) rot=(0,-1,0;1.5708rad)
  Solid = true
  Symmetric = false
FEATURE [Sketcher::SketchObject] Sketch024
  FullyConstrained = true
  sketch-geometry (7):
    g0: LineSegment StartX=0 StartY=0 StartZ=0 EndX=0 EndY=6 EndZ=0
    g1: Circle CenterX=0 CenterY=0 CenterZ=0 NormalX=0 NormalY=0 NormalZ=1 AngleXU=0 Radius=1
    g2: Circle CenterX=8 CenterY=6 CenterZ=0 NormalX=0 NormalY=0 NormalZ=1 AngleXU=0 Radius=1
    g3: BSplineCurve PolesCount=3 KnotsCount=2 Degree=2 IsPeriodic=0
    g4: GeomPoint X=0 Y=0 Z=0
    g5: GeomPoint X=8 Y=6 Z=0
    g6: LineSegment StartX=0 StartY=6 StartZ=0 EndX=8 EndY=6 EndZ=0
  constraints (14):
    c: Coincident(g0,g-1)
    c: Distance(g0) = 6
    c: Vertical(g0)
    c: Coincident(g3,g0)
    c: Weight(g1) = 1
    c: Equal(g1,g2)
    c: InternalAlignment(g1,g3)
    c: InternalAlignment(g2,g3)
    c: InternalAlignment(g4,g3)
    c: InternalAlignment(g5,g3)
    c: Block(g3)
    c: Coincident(g6,g0)
    c: Coincident(g6,g3)
    c: Horizontal(g6)
FEATURE [Part::Extrusion] Extrude018  label="caseScrewPillarBracket006"
  Base = -> Sketch024
  Dir = (0,0,1)
  DirMode = 2
  FaceMakerClass = Part::FaceMakerBullseye
  LengthFwd = 2.4
  LengthRev = 0
  Placement = pos=(103.7,29,6.77) rot=(0,-1,0;1.5708rad)
  Solid = true
  Symmetric = false
FEATURE [Sketcher::SketchObject] Sketch025
  FullyConstrained = true
  sketch-geometry (7):
    g0: LineSegment StartX=0 StartY=0 StartZ=0 EndX=0 EndY=6 EndZ=0
    g1: Circle CenterX=0 CenterY=0 CenterZ=0 NormalX=0 NormalY=0 NormalZ=1 AngleXU=0 Radius=1
    g2: Circle CenterX=8 CenterY=6 CenterZ=0 NormalX=0 NormalY=0 NormalZ=1 AngleXU=0 Radius=1
    g3: BSplineCurve PolesCount=3 KnotsCount=2 Degree=2 IsPeriodic=0
    g4: GeomPoint X=0 Y=0 Z=0
    g5: GeomPoint X=8 Y=6 Z=0
    g6: LineSegment StartX=0 StartY=6 StartZ=0 EndX=8 EndY=6 EndZ=0
  constraints (14):
    c: Coincident(g0,g-1)
    c: Distance(g0) = 6
    c: Vertical(g0)
    c: Coincident(g3,g0)
    c: Weight(g1) = 1
    c: Equal(g1,g2)
    c: InternalAlignment(g1,g3)
    c: InternalAlignment(g2,g3)
    c: InternalAlignment(g4,g3)
    c: InternalAlignment(g5,g3)
    c: Block(g3)
    c: Coincident(g6,g0)
    c: Coincident(g6,g3)
    c: Horizontal(g6)
FEATURE [Part::Extrusion] Extrude019  label="caseScrewPillarBracket007"
  Base = -> Sketch025
  Dir = (0,0,1)
  DirMode = 2
  FaceMakerClass = Part::FaceMakerBullseye
  LengthFwd = 2.4
  LengthRev = 0
  Placement = pos=(101.3,29,65.23) rot=(0,1,0;1.5708rad)
  Solid = true
  Symmetric = false
FEATURE [Part::Box] Box011  label="frontCaseScrewPillarBracket"
  AttacherType = Attacher::AttachEngine3D
  Height = 2.4
  Length = 16
  Placement = pos=(87,28,2.3) rot=(0,0,1;0rad)
  Width = 7
FEATURE [Part::Box] Box012  label="frontCaseScrewPillarBracket001"
  AttacherType = Attacher::AttachEngine3D
  Height = 2.4
  Length = 16
  Placement = pos=(87,28,67.3) rot=(0,0,1;0rad)
  Width = 7
FEATURE [Sketcher::SketchObject] Sketch026
  FullyConstrained = true
  sketch-geometry (17):
    g0: Circle CenterX=-3.5 CenterY=23.5 CenterZ=0 NormalX=0 NormalY=0 NormalZ=1 AngleXU=0 Radius=1
    g1: Circle CenterX=-1 CenterY=15.25 CenterZ=0 NormalX=0 NormalY=0 NormalZ=1 AngleXU=0 Radius=1
    g2: Circle CenterX=-3.5 CenterY=7 CenterZ=0 NormalX=0 NormalY=0 NormalZ=1 AngleXU=0 Radius=1
    g3: BSplineCurve PolesCount=3 KnotsCount=2 Degree=2 IsPeriodic=0
    g4: GeomPoint X=-3.5 Y=23.5 Z=0
    g5: GeomPoint X=-3.5 Y=7 Z=0
    g6: Circle CenterX=-4.8 CenterY=30.5 CenterZ=0 NormalX=0 NormalY=0 NormalZ=1 AngleXU=0 Radius=1
    g7: Circle CenterX=-3.5 CenterY=30.5 CenterZ=0 NormalX=0 NormalY=0 NormalZ=1 AngleXU=0 Radius=1
    g8: Circle CenterX=-3.5 CenterY=29.2 CenterZ=0 NormalX=0 NormalY=0 NormalZ=1 AngleXU=0 Radius=1
    g9: BSplineCurve PolesCount=3 KnotsCount=2 Degree=2 IsPeriodic=0
    g10: GeomPoint X=-4.8 Y=30.5 Z=0
    g11: GeomPoint X=-3.5 Y=29.2 Z=0
    g12: LineSegment StartX=-3.5 StartY=29.2 StartZ=0 EndX=-3.5 EndY=23.5 EndZ=0
    g13: LineSegment StartX=-4.8 StartY=30.5 StartZ=0 EndX=0 EndY=30.5 EndZ=0
    g14: LineSegment StartX=-3.5 StartY=5 StartZ=0 EndX=-3.5 EndY=7 EndZ=0
    g15: LineSegment StartX=0 StartY=5 StartZ=0 EndX=0 EndY=30.5 EndZ=0
    g16: LineSegment StartX=-3.5 StartY=5 StartZ=0 EndX=0 EndY=5 EndZ=0
  constraints (33):
    c: Weight(g0) = 1
    c: Equal(g0,g1)
    c: Equal(g0,g2)
    c: InternalAlignment(g0,g3)
    c: InternalAlignment(g1,g3)
    c: InternalAlignment(g2,g3)
    c: InternalAlignment(g4,g3)
    c: InternalAlignment(g5,g3)
    c: Block(g3)
    c: Weight(g6) = 1
    c: Equal(g6,g7)
    c: Equal(g6,g8)
    c: InternalAlignment(g6,g9)
    c: InternalAlignment(g7,g9)
    c: InternalAlignment(g8,g9)
    c: InternalAlignment(g10,g9)
    c: InternalAlignment(g11,g9)
    c: Block(g9)
    c: Coincident(g12,g9)
    c: Coincident(g12,g3)
    c: Vertical(g12)
    c: Coincident(g13,g9)
    c: Horizontal(g13)
    c: Distance(g13) = 4.8
    c: Coincident(g14,g3)
    c: Vertical(g14)
    c: Coincident(g15,g13)
    c: Vertical(g15)
    c: Tangent(g15,g1)
    c: Distance(g14) = 2
    c: Coincident(g16,g14)
    c: Horizontal(g16)
    c: Coincident(g15,g16)
FEATURE [Part::Feature] Face050
  shape: bbox 4.8 x 25.5 x 2e-07 mm, 1 faces, 0 solids (baked)
FEATURE [Part::Revolution] Revolve054  label="moreFrontCaseScrewPost001"
  Angle = 360
  Axis = (0,1,0)
  Base = (0,0,0)
  FaceMakerClass = Part::FaceMakerBullseye
  Placement = pos=(102.5,4.5,3.5) rot=(0,0,1;0rad)
  Solid = false
  Source = -> Face050
  Symmetric = false
FEATURE [Part::Feature] Face051
  shape: bbox 4.8 x 25.5 x 2e-07 mm, 1 faces, 0 solids (baked)
FEATURE [Part::Revolution] Revolve055  label="moreFrontCaseScrewPost002"
  Angle = 360
  Axis = (0,1,0)
  Base = (0,0,0)
  FaceMakerClass = Part::FaceMakerBullseye
  Placement = pos=(102.5,4.5,68.5) rot=(0,0,1;0rad)
  Solid = false
  Source = -> Face051
  Symmetric = false
FEATURE [Sketcher::SketchObject] Sketch027
  FullyConstrained = true
  sketch-geometry (10):
    g0: LineSegment StartX=-1.6 StartY=4.7 StartZ=0 EndX=-1.6 EndY=1.7 EndZ=0
    g1: LineSegment StartX=-3.5 StartY=4.7 StartZ=0 EndX=-1.6 EndY=4.7 EndZ=0
    g2: LineSegment StartX=-1.6 StartY=1.7 StartZ=0 EndX=-1.6 EndY=1.5 EndZ=0
    g3: LineSegment StartX=-1.6 StartY=1.5 StartZ=0 EndX=-5.2 EndY=1.5 EndZ=0
    g4: Circle CenterX=-3.5 CenterY=4.7 CenterZ=0 NormalX=0 NormalY=0 NormalZ=1 AngleXU=0 Radius=1
    g5: Circle CenterX=-3.59627 CenterY=2.99743 CenterZ=0 NormalX=0 NormalY=0 NormalZ=1 AngleXU=0 Radius=1
    g6: Circle CenterX=-5.2 CenterY=1.5 CenterZ=0 NormalX=0 NormalY=0 NormalZ=1 AngleXU=0 Radius=1
    g7: BSplineCurve PolesCount=3 KnotsCount=2 Degree=2 IsPeriodic=0
    g8: GeomPoint X=-3.5 Y=4.7 Z=0
    g9: GeomPoint X=-5.2 Y=1.5 Z=0
  constraints (23):
    c: Vertical(g0)
    c: Distance(g0) = 3
    c: Coincident(g1,g0)
    c: Horizontal(g1)
    c: Block(g0)
    c: Block(g1)
    c: Coincident(g2,g0)
    c: Vertical(g2)
    c: Distance(g2) = 0.2
    c: Coincident(g3,g2)
    c: Horizontal(g3)
    c: Block(g3)
    c: Coincident(g7,g1)
    c: Weight(g4) = 1
    c: Equal(g4,g5)
    c: Equal(g4,g6)
    c: Coincident(g7,g3)
    c: InternalAlignment(g4,g7)
    c: InternalAlignment(g5,g7)
    c: InternalAlignment(g6,g7)
    c: InternalAlignment(g8,g7)
    c: InternalAlignment(g9,g7)
    c: Block(g7)
FEATURE [Sketcher::SketchObject] Sketch028
  FullyConstrained = true
  sketch-geometry (18):
    g0: LineSegment StartX=0 StartY=3e-16 StartZ=0 EndX=0 EndY=1.7 EndZ=0
    g1: LineSegment StartX=-3.5 StartY=0 StartZ=0 EndX=-3.5 EndY=0.9 EndZ=0
    g2: Circle CenterX=-2.7 CenterY=1.7 CenterZ=0 NormalX=0 NormalY=0 NormalZ=1 AngleXU=0 Radius=1
    g3: Circle CenterX=-3.5 CenterY=1.7 CenterZ=0 NormalX=0 NormalY=0 NormalZ=1 AngleXU=0 Radius=1
    g4: Circle CenterX=-3.5 CenterY=0.9 CenterZ=0 NormalX=0 NormalY=0 NormalZ=1 AngleXU=0 Radius=1
    g5: BSplineCurve PolesCount=3 KnotsCount=2 Degree=2 IsPeriodic=0
    g6: GeomPoint X=-2.7 Y=1.7 Z=0
    g7: GeomPoint X=-3.5 Y=0.9 Z=0
    g8: LineSegment StartX=-3.5 StartY=0 StartZ=0 EndX=-3.5 EndY=-7 EndZ=0
    g9: LineSegment StartX=0 StartY=3e-16 StartZ=0 EndX=0 EndY=-7 EndZ=0
    g10: LineSegment StartX=-3.5 StartY=-7 StartZ=0 EndX=0 EndY=-7 EndZ=0
    g11: LineSegment StartX=-2.7 StartY=1.7 StartZ=0 EndX=-1.6 EndY=1.7 EndZ=0
    g12: LineSegment StartX=0 StartY=1.7 StartZ=0 EndX=0 EndY=4.5 EndZ=0
    g13: LineSegment StartX=0 StartY=4.5 StartZ=0 EndX=0 EndY=10.8 EndZ=0
    g14: LineSegment StartX=0 StartY=10.8 StartZ=0 EndX=-2 EndY=10.8 EndZ=0
    g15: LineSegment StartX=-1.6 StartY=4.7 StartZ=0 EndX=-1.6 EndY=1.7 EndZ=0
    g16: LineSegment StartX=-1.6 StartY=4.7 StartZ=0 EndX=-2 EndY=4.7 EndZ=0
    g17: LineSegment StartX=-2 StartY=4.7 StartZ=0 EndX=-2 EndY=10.8 EndZ=0
  constraints (44):
    c: Vertical(g0)
    c: Vertical(g1)
    c: Distance(g1) = 0.9
    c: Block(g0)
    c: Distance(g0) = 1.7
    c: Weight(g2) = 1
    c: Equal(g2,g3)
    c: Equal(g2,g4)
    c: Coincident(g5,g1)
    c: InternalAlignment(g2,g5)
    c: InternalAlignment(g3,g5)
    c: InternalAlignment(g4,g5)
    c: InternalAlignment(g6,g5)
    c: InternalAlignment(g7,g5)
    c: Block(g5)
    c: Coincident(g8,g1)
    c: Vertical(g8)
    c: Distance(g8) = 7
    c: Vertical(g9)
    c: Equal(g8,g9) = 7
    c: Coincident(g9,g0)
    c: Coincident(g10,g8)
    c: Coincident(g10,g9)
    c: Horizontal(g10)
    c: Coincident(g11,g5)
    c: Horizontal(g11)
    c: Coincident(g12,g0)
    c: Vertical(g12)
    c: Distance(g12) = 2.8
    c: Coincident(g13,g12)
    c: Vertical(g13)
    c: Distance(g13) = 6.3
    c: Coincident(g14,g13)
    c: Horizontal(g14)
    c: Distance(g14) = 2
    c: Vertical(g15)
    c: Distance(g15) = 3
    c: Block(g11)
    c: Coincident(g15,g11)
    c: Coincident(g16,g15)
    c: Horizontal(g16)
    c: Coincident(g17,g16)
    c: Coincident(g17,g14)
    c: Vertical(g17)
FEATURE [Part::Revolution] Revolve040  label="backCaseScrewRetainer001"
  Angle = 360
  Axis = (0,1,0)
  Base = (0,0,0)
  FaceMakerClass = Part::FaceMakerBullseye
  Placement = pos=(12.5,3,10) rot=(0,0,1;0rad)
  Solid = false
  Source = -> Face036
  Symmetric = false
FEATURE [Part::Feature] Face055
  shape: bbox 3.5 x 30.2 x 2e-07 mm, 1 faces, 0 solids (baked)
FEATURE [Part::Revolution] Revolve059  label="backCaseScrewPost"
  Angle = 360
  Axis = (0,1,0)
  Base = (0,0,0)
  FaceMakerClass = Part::FaceMakerBullseye
  Placement = pos=(12.5,4.5,10) rot=(0,0,1;0rad)
  Solid = false
  Source = -> Face055
  Symmetric = false
FEATURE [Part::Feature] Face056
  shape: bbox 3.5 x 30.2 x 2e-07 mm, 1 faces, 0 solids (baked)
FEATURE [Part::Revolution] Revolve060  label="backCaseScrewPost001"
  Angle = 360
  Axis = (0,1,0)
  Base = (0,0,0)
  FaceMakerClass = Part::FaceMakerBullseye
  Placement = pos=(12.5,4.5,62) rot=(0,0,1;0rad)
  Solid = false
  Source = -> Face056
  Symmetric = false
FEATURE [Part::Feature] Face057
  shape: bbox 3.5 x 17.8 x 2e-07 mm, 1 faces, 0 solids (baked)
FEATURE [Part::Revolution] Revolve061  label="removeToCreateScrewAndThreadedInsertHole"
  Angle = 360
  Axis = (0,1,0)
  Base = (0,0,0)
  FaceMakerClass = Part::FaceMakerBullseye
  Placement = pos=(12.5,0,10) rot=(0,0,1;0rad)
  Solid = false
  Source = -> Face057
  Symmetric = false
FEATURE [Part::Feature] Face058
  shape: bbox 3.5 x 17.8 x 2e-07 mm, 1 faces, 0 solids (baked)
FEATURE [Part::Revolution] Revolve062  label="removeToCreateScrewAndThreadedInsertHole001"
  Angle = 360
  Axis = (0,1,0)
  Base = (0,0,0)
  FaceMakerClass = Part::FaceMakerBullseye
  Placement = pos=(12.5,0,62) rot=(0,0,1;0rad)
  Solid = false
  Source = -> Face058
  Symmetric = false
FEATURE [Part::Feature] Face059
  shape: bbox 3.5 x 17.8 x 2e-07 mm, 1 faces, 0 solids (baked)
FEATURE [Part::Revolution] Revolve063  label="removeToCreateScrewAndThreadedInsertHole002"
  Angle = 360
  Axis = (0,1,0)
  Base = (0,0,0)
  FaceMakerClass = Part::FaceMakerBullseye
  Placement = pos=(89.5,0,68.5) rot=(0,0,1;0rad)
  Solid = false
  Source = -> Face059
  Symmetric = false
FEATURE [Part::Feature] Face060
  shape: bbox 3.5 x 17.8 x 2e-07 mm, 1 faces, 0 solids (baked)
FEATURE [Part::Revolution] Revolve064  label="removeToCreateScrewAndThreadedInsertHole003"
  Angle = 360
  Axis = (0,1,0)
  Base = (0,0,0)
  FaceMakerClass = Part::FaceMakerBullseye
  Placement = pos=(89.5,0,3.5) rot=(0,0,1;0rad)
  Solid = false
  Source = -> Face060
  Symmetric = false
FEATURE [Part::Feature] Face061
  shape: bbox 3.5 x 17.8 x 2e-07 mm, 1 faces, 0 solids (baked)
FEATURE [Part::Revolution] Revolve065  label="removeToCreateScrewAndThreadedInsertHole004"
  Angle = 360
  Axis = (0,1,0)
  Base = (0,0,0)
  FaceMakerClass = Part::FaceMakerBullseye
  Placement = pos=(102.5,4.7,3.5) rot=(0,0,1;0rad)
  Solid = false
  Source = -> Face061
  Symmetric = false
FEATURE [Part::Feature] Face062
  shape: bbox 3.5 x 17.8 x 2e-07 mm, 1 faces, 0 solids (baked)
FEATURE [Part::Revolution] Revolve066  label="removeToCreateScrewAndThreadedInsertHole005"
  Angle = 360
  Axis = (0,1,0)
  Base = (0,0,0)
  FaceMakerClass = Part::FaceMakerBullseye
  Placement = pos=(102.5,4.7,68.5) rot=(0,0,1;0rad)
  Solid = false
  Source = -> Face062
  Symmetric = false
FEATURE [Part::MultiFuse] Fusion047  label="makeHoles"
  Shapes = -> [Revolve066,Revolve065,Revolve064,Revolve063,Revolve062,Revolve061]
FEATURE [Part::Feature] Face063
  shape: bbox 3.6 x 3.2 x 2e-07 mm, 1 faces, 0 solids (baked)
FEATURE [Part::Revolution] Revolve067  label="moreFrontCaseScrewRetainer002"
  Angle = 360
  Axis = (0,1,0)
  Base = (0,0,0)
  FaceMakerClass = Part::FaceMakerBullseye
  Placement = pos=(102.5,4.5,68.5) rot=(0,0,1;0rad)
  Solid = false
  Source = -> Face063
  Symmetric = false
FEATURE [Part::Feature] Face064
  shape: bbox 3.6 x 3.2 x 2e-07 mm, 1 faces, 0 solids (baked)
FEATURE [Part::Revolution] Revolve068  label="moreFrontCaseScrewRetainer003"
  Angle = 360
  Axis = (0,1,0)
  Base = (0,0,0)
  FaceMakerClass = Part::FaceMakerBullseye
  Placement = pos=(102.5,4.5,3.5) rot=(0,0,1;0rad)
  Solid = false
  Source = -> Face064
  Symmetric = false
FEATURE [Part::Feature] Face065
  shape: bbox 3.5 x 17.8 x 2e-07 mm, 1 faces, 0 solids (baked)
FEATURE [Part::Revolution] Revolve069  label="removeToCreateScrewAndThreadedInsertHole006"
  Angle = 360
  Axis = (0,1,0)
  Base = (0,0,0)
  FaceMakerClass = Part::FaceMakerBullseye
  Placement = pos=(12.5,0,10) rot=(0,0,1;0rad)
  Solid = false
  Source = -> Face065
  Symmetric = false
FEATURE [Part::Feature] Face066
  shape: bbox 3.5 x 17.8 x 2e-07 mm, 1 faces, 0 solids (baked)
FEATURE [Part::Revolution] Revolve070  label="removeToCreateScrewAndThreadedInsertHole007"
  Angle = 360
  Axis = (0,1,0)
  Base = (0,0,0)
  FaceMakerClass = Part::FaceMakerBullseye
  Placement = pos=(12.5,0,62) rot=(0,0,1;0rad)
  Solid = false
  Source = -> Face066
  Symmetric = false
FEATURE [Part::Feature] Face067
  shape: bbox 3.5 x 17.8 x 2e-07 mm, 1 faces, 0 solids (baked)
FEATURE [Part::Revolution] Revolve071  label="removeToCreateScrewAndThreadedInsertHole008"
  Angle = 360
  Axis = (0,1,0)
  Base = (0,0,0)
  FaceMakerClass = Part::FaceMakerBullseye
  Placement = pos=(89.5,0,68.5) rot=(0,0,1;0rad)
  Solid = false
  Source = -> Face067
  Symmetric = false
FEATURE [Part::Feature] Face068
  shape: bbox 3.5 x 17.8 x 2e-07 mm, 1 faces, 0 solids (baked)
FEATURE [Part::Revolution] Revolve072  label="removeToCreateScrewAndThreadedInsertHole009"
  Angle = 360
  Axis = (0,1,0)
  Base = (0,0,0)
  FaceMakerClass = Part::FaceMakerBullseye
  Placement = pos=(89.5,0,3.5) rot=(0,0,1;0rad)
  Solid = false
  Source = -> Face068
  Symmetric = false
FEATURE [Part::Feature] Face069
  shape: bbox 3.5 x 17.8 x 2e-07 mm, 1 faces, 0 solids (baked)
FEATURE [Part::Feature] Face070
  shape: bbox 3.5 x 17.8 x 2e-07 mm, 1 faces, 0 solids (baked)
FEATURE [Part::Revolution] Revolve073  label="removeToCreateScrewAndThreadedInsertHole010"
  Angle = 360
  Axis = (0,1,0)
  Base = (0,0,0)
  FaceMakerClass = Part::FaceMakerBullseye
  Placement = pos=(102.5,4.7,3.5) rot=(0,0,1;0rad)
  Solid = false
  Source = -> Face069
  Symmetric = false
FEATURE [Part::Revolution] Revolve074  label="removeToCreateScrewAndThreadedInsertHole011"
  Angle = 360
  Axis = (0,1,0)
  Base = (0,0,0)
  FaceMakerClass = Part::FaceMakerBullseye
  Placement = pos=(102.5,4.7,68.5) rot=(0,0,1;0rad)
  Solid = false
  Source = -> Face070
  Symmetric = false
FEATURE [Part::MultiFuse] Fusion048  label="makeHoles001"
  Shapes = -> [Revolve074,Revolve073,Revolve072,Revolve071,Revolve070,Revolve069]
FEATURE [Part::MultiFuse] Fusion049  label="caseScrewRetainers"
  Shapes = -> [Revolve067,Revolve068,Revolve048,Revolve047,Revolve039,Revolve040]
FEATURE [Part::Cut] Cut015  label="caseScrewRetainers001"
  Base = -> Fusion049
  Tool = -> Fusion048
FEATURE [Part::MultiFuse] Fusion050  label="casePillars"
  Shapes = -> [Revolve055,Revolve054,Revolve043,Revolve046,Revolve059,Revolve060]
FEATURE [Part::Feature] Face071 .. Face076  x6 (patterned run collapsed; names and placements below)
  shape: bbox 3.5 x 17.8 x 2e-07 mm, 1 faces, 0 solids (baked)
FEATURE [Part::Revolution] Revolve075  label="removeToCreateScrewAndThreadedInsertHole012"
  Angle = 360
  Axis = (0,1,0)
  Base = (0,0,0)
  FaceMakerClass = Part::FaceMakerBullseye
  Placement = pos=(12.5,0,10) rot=(0,0,1;0rad)
  Solid = false
  Source = -> Face071
  Symmetric = false
FEATURE [Part::Revolution] Revolve076  label="removeToCreateScrewAndThreadedInsertHole013"
  Angle = 360
  Axis = (0,1,0)
  Base = (0,0,0)
  FaceMakerClass = Part::FaceMakerBullseye
  Placement = pos=(12.5,0,62) rot=(0,0,1;0rad)
  Solid = false
  Source = -> Face072
  Symmetric = false
FEATURE [Part::Revolution] Revolve077  label="removeToCreateScrewAndThreadedInsertHole014"
  Angle = 360
  Axis = (0,1,0)
  Base = (0,0,0)
  FaceMakerClass = Part::FaceMakerBullseye
  Placement = pos=(89.5,0,68.5) rot=(0,0,1;0rad)
  Solid = false
  Source = -> Face073
  Symmetric = false
FEATURE [Part::Revolution] Revolve078  label="removeToCreateScrewAndThreadedInsertHole015"
  Angle = 360
  Axis = (0,1,0)
  Base = (0,0,0)
  FaceMakerClass = Part::FaceMakerBullseye
  Placement = pos=(89.5,0,3.5) rot=(0,0,1;0rad)
  Solid = false
  Source = -> Face074
  Symmetric = false
FEATURE [Part::Revolution] Revolve079  label="removeToCreateScrewAndThreadedInsertHole016"
  Angle = 360
  Axis = (0,1,0)
  Base = (0,0,0)
  FaceMakerClass = Part::FaceMakerBullseye
  Placement = pos=(102.5,4.7,3.5) rot=(0,0,1;0rad)
  Solid = false
  Source = -> Face075
  Symmetric = false
FEATURE [Part::Revolution] Revolve080  label="removeToCreateScrewAndThreadedInsertHole017"
  Angle = 360
  Axis = (0,1,0)
  Base = (0,0,0)
  FaceMakerClass = Part::FaceMakerBullseye
  Placement = pos=(102.5,4.7,68.5) rot=(0,0,1;0rad)
  Solid = false
  Source = -> Face076
  Symmetric = false
FEATURE [Part::MultiFuse] Fusion051  label="makeHoles002"
  Shapes = -> [Revolve080,Revolve079,Revolve078,Revolve077,Revolve076,Revolve075]
FEATURE [Part::Cut] Cut016  label="caesPillars"
  Base = -> Fusion050
  Tool = -> Fusion051
FEATURE [Part::Revolution] Revolve009  label="plugHousing016"
  Angle = 360
  Axis = (0,1,0)
  Base = (0,0,0)
  FaceMakerClass = Part::FaceMakerBullseye
  Placement = pos=(0,0,36.15) rot=(0,0,1;0rad)
  Solid = false
  Source = -> Face012
  Symmetric = false
FEATURE [Part::MultiFuse] Fusion014  label="plugHousing023"
  Placement = pos=(0,0,0) rot=(0,0,1;1.5708rad)
  Shapes = -> [Revolve011,Revolve009]
FEATURE [Part::Revolution] Revolve010  label="plugHousing017"
  Angle = 360
  Axis = (0,1,0)
  Base = (0,0,0)
  FaceMakerClass = Part::FaceMakerBullseye
  Placement = pos=(0,0,36.15) rot=(0,0,1;0rad)
  Solid = false
  Source = -> Face014
  Symmetric = false
FEATURE [Part::MultiFuse] Fusion015  label="plugHousing024"
  Placement = pos=(0,0,0) rot=(0,0,1;1.5708rad)
  Shapes = -> [Revolve010,Revolve015]
FEATURE [Part::Revolution] Revolve014  label="plugHousing026"
  Angle = 360
  Axis = (0,1,0)
  Base = (0,0,0)
  FaceMakerClass = Part::FaceMakerBullseye
  Placement = pos=(0,0,36.15) rot=(0,0,1;0rad)
  Solid = false
  Source = -> Face011
  Symmetric = false
FEATURE [Part::Revolution] Revolve013  label="plugHousing025"
  Angle = 360
  Axis = (0,1,0)
  Base = (0,0,0)
  FaceMakerClass = Part::FaceMakerBullseye
  Placement = pos=(0,0,36.15) rot=(0,0,1;0rad)
  Solid = false
  Source = -> Face015
  Symmetric = false
FEATURE [Part::MultiFuse] Fusion016  label="plugHousing028"
  Placement = pos=(0,19,0) rot=(0,0,1;3.14159rad)
  Shapes = -> [Fusion014,Fusion013]
FEATURE [Part::MultiFuse] Fusion011  label="plugHousing018"
  Placement = pos=(0,0,0) rot=(0,0,1;1.5708rad)
  Shapes = -> [Revolve014,Revolve013]
FEATURE [Part::MultiFuse] Fusion012  label="plugHousing019"
  Placement = pos=(0,19,0) rot=(0,0,1;3.14159rad)
  Shapes = -> [Fusion011,Fusion015]
FEATURE [Part::MultiFuse] Fusion017  label="plugHousing029"
  Placement = pos=(122.621,0,-0.15) rot=(0,0,1;0rad)
  Shapes = -> [Fusion016,Fusion012]
FEATURE [Part::MultiFuse] Fusion052  label="casePillarRetainers"
  Shapes = -> [Extrude012,Extrude013,Extrude014,Extrude015,Extrude016,Extrude017,Extrude018,Extrude019,Box011,Box012]
FEATURE [Part::Feature] Face077
  shape: bbox 3.5 x 17.8 x 2e-07 mm, 1 faces, 0 solids (baked)
FEATURE [Part::Revolution] Revolve081  label="removeToCreateScrewAndThreadedInsertHole018"
  Angle = 360
  Axis = (0,1,0)
  Base = (0,0,0)
  FaceMakerClass = Part::FaceMakerBullseye
  Placement = pos=(62.3,30.3,19.7) rot=(0,0,1;0rad)
  Solid = false
  Source = -> Face077
  Symmetric = false
FEATURE [Part::Feature] Face078
  shape: bbox 3.5 x 17.8 x 2e-07 mm, 1 faces, 0 solids (baked)
FEATURE [Part::Revolution] Revolve082  label="removeToCreateScrewAndThreadedInsertHole019"
  Angle = 360
  Axis = (0,1,0)
  Base = (0,0,0)
  FaceMakerClass = Part::FaceMakerBullseye
  Placement = pos=(62.3,30.3,51.7) rot=(0,0,1;0rad)
  Solid = false
  Source = -> Face078
  Symmetric = false
FEATURE [Part::Feature] Face079
  shape: bbox 3.5 x 17.8 x 2e-07 mm, 1 faces, 0 solids (baked)
FEATURE [Part::Revolution] Revolve083  label="removeToCreateScrewAndThreadedInsertHole020"
  Angle = 360
  Axis = (0,1,0)
  Base = (0,0,0)
  FaceMakerClass = Part::FaceMakerBullseye
  Placement = pos=(30.3,30.3,19.7) rot=(0,0,1;0rad)
  Solid = false
  Source = -> Face079
  Symmetric = false
FEATURE [Part::Feature] Face080
  shape: bbox 3.5 x 17.8 x 2e-07 mm, 1 faces, 0 solids (baked)
FEATURE [Part::Revolution] Revolve084  label="removeToCreateScrewAndThreadedInsertHole021"
  Angle = 360
  Axis = (0,1,0)
  Base = (0,0,0)
  FaceMakerClass = Part::FaceMakerBullseye
  Placement = pos=(30.3,30.3,51.7) rot=(0,0,1;0rad)
  Solid = false
  Source = -> Face080
  Symmetric = false
FEATURE [Part::MultiFuse] Fusion053  label="createThreadedInsertHolesForFan"
  Shapes = -> [Revolve081,Revolve082,Revolve083,Revolve084]
FEATURE [Part::Cut] Cut017  label="fanScrewHousing001"
  Base = -> Fusion046
  Tool = -> Fusion053
FEATURE [Part::Feature] Face081
  shape: bbox 3.5 x 17.8 x 2e-07 mm, 1 faces, 0 solids (baked)
FEATURE [Part::Revolution] Revolve085  label="removeToCreateScrewAndThreadedInsertHole022"
  Angle = 360
  Axis = (0,1,0)
  Base = (0,0,0)
  FaceMakerClass = Part::FaceMakerBullseye
  Placement = pos=(62.3,30.3,19.7) rot=(0,0,1;0rad)
  Solid = false
  Source = -> Face081
  Symmetric = false
FEATURE [Part::Feature] Face082
  shape: bbox 3.5 x 17.8 x 2e-07 mm, 1 faces, 0 solids (baked)
FEATURE [Part::Revolution] Revolve086  label="removeToCreateScrewAndThreadedInsertHole023"
  Angle = 360
  Axis = (0,1,0)
  Base = (0,0,0)
  FaceMakerClass = Part::FaceMakerBullseye
  Placement = pos=(62.3,30.3,51.7) rot=(0,0,1;0rad)
  Solid = false
  Source = -> Face082
  Symmetric = false
FEATURE [Part::Feature] Face083
  shape: bbox 3.5 x 17.8 x 2e-07 mm, 1 faces, 0 solids (baked)
FEATURE [Part::Revolution] Revolve087  label="removeToCreateScrewAndThreadedInsertHole024"
  Angle = 360
  Axis = (0,1,0)
  Base = (0,0,0)
  FaceMakerClass = Part::FaceMakerBullseye
  Placement = pos=(30.3,30.3,19.7) rot=(0,0,1;0rad)
  Solid = false
  Source = -> Face083
  Symmetric = false
FEATURE [Part::Feature] Face084
  shape: bbox 3.5 x 17.8 x 2e-07 mm, 1 faces, 0 solids (baked)
FEATURE [Part::Revolution] Revolve088  label="removeToCreateScrewAndThreadedInsertHole025"
  Angle = 360
  Axis = (0,1,0)
  Base = (0,0,0)
  FaceMakerClass = Part::FaceMakerBullseye
  Placement = pos=(30.3,30.3,51.7) rot=(0,0,1;0rad)
  Solid = false
  Source = -> Face084
  Symmetric = false
FEATURE [Part::MultiFuse] Fusion054  label="createThreadedInsertHolesForFan001"
  Shapes = -> [Revolve085,Revolve086,Revolve087,Revolve088]
FEATURE [Part::Cut] Cut018  label="top007"
  Base = -> Fusion040
  Tool = -> Fusion054
FEATURE [Sketcher::SketchObject] Sketch029
  FullyConstrained = false
  Placement = pos=(0,0,0) rot=(1,0,0;1.5708rad)
  sketch-geometry (24):
    g0: ArcOfCircle CenterX=-4 CenterY=-10.5 CenterZ=0 NormalX=0 NormalY=0 NormalZ=1 AngleXU=0 Radius=1.5 StartAngle=6e-16 EndAngle=3.14159
    g1: ArcOfCircle CenterX=-34.2 CenterY=-10.5 CenterZ=0 NormalX=0 NormalY=0 NormalZ=1 AngleXU=0 Radius=1.5 StartAngle=0 EndAngle=3.14159
    g2: ArcOfCircle CenterX=-34.2 CenterY=-27.7 CenterZ=0 NormalX=0 NormalY=0 NormalZ=1 AngleXU=0 Radius=1.5 StartAngle=3.14159 EndAngle=6.28319
    g3: ArcOfCircle CenterX=-4 CenterY=-27.7 CenterZ=0 NormalX=0 NormalY=0 NormalZ=1 AngleXU=0 Radius=1.5 StartAngle=3.1416 EndAngle=6.28319
    g4: ArcOfCircle CenterX=-10 CenterY=-4.3 CenterZ=0 NormalX=0 NormalY=0 NormalZ=1 AngleXU=0 Radius=1.5 StartAngle=2e-16 EndAngle=3.14159
    g5: ArcOfCircle CenterX=-16.1 CenterY=-1.8 CenterZ=0 NormalX=0 NormalY=0 NormalZ=1 AngleXU=0 Radius=1.5 StartAngle=5e-16 EndAngle=3.14159
    g6: ArcOfCircle CenterX=-22.1 CenterY=-1.8 CenterZ=0 NormalX=0 NormalY=0 NormalZ=1 AngleXU=0 Radius=1.5 StartAngle=5e-16 EndAngle=3.14159
    g7: ArcOfCircle CenterX=-28.2 CenterY=-4.3 CenterZ=0 NormalX=0 NormalY=0 NormalZ=1 AngleXU=0 Radius=1.5 StartAngle=2e-16 EndAngle=3.14159
    g8: ArcOfCircle CenterX=-10 CenterY=-33.9 CenterZ=0 NormalX=0 NormalY=0 NormalZ=1 AngleXU=0 Radius=1.5 StartAngle=3.14159 EndAngle=6.28319
    g9: ArcOfCircle CenterX=-16.1 CenterY=-36.4 CenterZ=0 NormalX=0 NormalY=0 NormalZ=1 AngleXU=0 Radius=1.5 StartAngle=3.14159 EndAngle=6.28319
    g10: ArcOfCircle CenterX=-22.1 CenterY=-36.4 CenterZ=0 NormalX=0 NormalY=0 NormalZ=1 AngleXU=0 Radius=1.5 StartAngle=3.14159 EndAngle=6.28319
    g11: ArcOfCircle CenterX=-28.2 CenterY=-33.9 CenterZ=0 NormalX=0 NormalY=0 NormalZ=1 AngleXU=0 Radius=1.5 StartAngle=3.14159 EndAngle=6.28319
    g12: LineSegment StartX=-35.7 StartY=-10.5 StartZ=0 EndX=-35.7 EndY=-27.7 EndZ=0
    g13: LineSegment StartX=-32.7 StartY=-10.5 StartZ=0 EndX=-32.7 EndY=-27.7 EndZ=0
    g14: LineSegment StartX=-29.7 StartY=-33.9 StartZ=0 EndX=-29.7 EndY=-4.3 EndZ=0
    g15: LineSegment StartX=-26.7 StartY=-33.9 StartZ=0 EndX=-26.7 EndY=-4.3 EndZ=0
    g16: LineSegment StartX=-2.5 StartY=-10.5 StartZ=0 EndX=-2.5 EndY=-27.7 EndZ=0
    g17: LineSegment StartX=-8.5 StartY=-4.3 StartZ=0 EndX=-8.5 EndY=-33.9 EndZ=0
    g18: LineSegment StartX=-5.5 StartY=-10.5 StartZ=0 EndX=-5.5 EndY=-27.7 EndZ=0
    g19: LineSegment StartX=-11.5 StartY=-4.3 StartZ=0 EndX=-11.5 EndY=-33.9 EndZ=0
    g20: LineSegment StartX=-14.6 StartY=-1.8 StartZ=0 EndX=-14.6 EndY=-36.4 EndZ=0
    g21: LineSegment StartX=-17.6 StartY=-1.8 StartZ=0 EndX=-17.6 EndY=-36.4 EndZ=0
    g22: LineSegment StartX=-20.6 StartY=-36.4 StartZ=0 EndX=-20.6 EndY=-1.8 EndZ=0
    g23: LineSegment StartX=-23.6 StartY=-1.8 StartZ=0 EndX=-23.6 EndY=-36.4 EndZ=0
  constraints (48):
    c: Block(g0)
    c: Block(g1)
    c: Block(g2)
    c: Block(g3)
    c: Block(g4)
    c: Block(g5)
    c: Block(g6)
    c: Block(g7)
    c: Block(g8)
    c: Block(g9)
    c: Block(g10)
    c: Block(g11)
    c: Coincident(g12,g1)
    c: Coincident(g12,g2)
    c: Vertical(g12)
    c: Coincident(g13,g1)
    c: Coincident(g13,g2)
    c: Vertical(g13)
    c: Coincident(g14,g11)
    c: Coincident(g14,g7)
    c: Vertical(g14)
    c: Coincident(g15,g11)
    c: Coincident(g15,g7)
    c: Vertical(g15)
    c: Coincident(g16,g0)
    c: Coincident(g16,g3)
    c: Vertical(g16)
    c: Coincident(g17,g4)
    c: Coincident(g17,g8)
    c: Vertical(g17)
    c: Coincident(g18,g0)
    c: Coincident(g18,g3)
    c: Vertical(g18)
    c: Coincident(g19,g4)
    c: Coincident(g19,g8)
    c: Vertical(g19)
    c: Coincident(g20,g5)
    c: Coincident(g20,g9)
    c: Vertical(g20)
    c: Coincident(g21,g5)
    c: Coincident(g21,g9)
    c: Vertical(g21)
    c: Coincident(g22,g10)
    c: Coincident(g22,g6)
    c: Vertical(g22)
    c: Coincident(g23,g6)
    c: Coincident(g23,g10)
    c: Vertical(g23)
FEATURE [Part::Extrusion] Extrude020  label="removeToCreateFanGrillHoles"
  Base = -> Sketch029
  Dir = (0,-1,6e-16)
  DirMode = 2
  FaceMakerClass = Part::FaceMakerBullseye
  LengthFwd = 10
  LengthRev = 0
  Placement = pos=(65.4,44,54.82) rot=(0,0,1;0rad)
  Solid = true
  Symmetric = false
FEATURE [Part::MultiFuse] Fusion055  label="top008"
  Shapes = -> [Cut017,Cut018]
FEATURE [Part::Cut] Cut019  label="top009"
  Base = -> Fusion055
  Tool = -> Extrude020
FEATURE [App::MeasureDistance] Distance003  label="Distance: 71.95 mm"
  Distance = 71.9513
  P1 = (117,38,72)
  P2 = (117,38,0.0487319)
FEATURE [Sketcher::SketchObject] Sketch030
  FullyConstrained = true
  Placement = pos=(117,19,0) rot=(0.57735,0.57735,0.57735;2.0944rad)
  sketch-geometry (48):
    g0: LineSegment StartX=-49.19 StartY=69.25 StartZ=0 EndX=-49.19 EndY=66.25 EndZ=0
    g1: LineSegment StartX=-49.19 StartY=63.5 StartZ=0 EndX=-49.19 EndY=60.5 EndZ=0
    g2: LineSegment StartX=-49.19 StartY=57.75 StartZ=0 EndX=-49.19 EndY=54.75 EndZ=0
    g3: LineSegment StartX=-49.19 StartY=52 StartZ=0 EndX=-49.19 EndY=49 EndZ=0
    g4: LineSegment StartX=-49.19 StartY=46.25 StartZ=0 EndX=-49.19 EndY=43.25 EndZ=0
    g5: LineSegment StartX=-49.19 StartY=40.5 StartZ=0 EndX=-49.19 EndY=37.5 EndZ=0
    g6: LineSegment StartX=-49.19 StartY=34.5 StartZ=0 EndX=-49.19 EndY=31.5 EndZ=0
    g7: LineSegment StartX=-49.19 StartY=28.75 StartZ=0 EndX=-49.19 EndY=25.75 EndZ=0
    g8: LineSegment StartX=-49.19 StartY=23 StartZ=0 EndX=-49.19 EndY=20 EndZ=0
    g9: LineSegment StartX=-49.19 StartY=17.25 StartZ=0 EndX=-49.19 EndY=14.25 EndZ=0
    g10: LineSegment StartX=-49.19 StartY=11.5 StartZ=0 EndX=-49.19 EndY=8.5 EndZ=0
    g11: LineSegment StartX=-49.19 StartY=5.75 StartZ=0 EndX=-49.19 EndY=2.75 EndZ=0
    g12: ArcOfCircle CenterX=-1.5 CenterY=67.75 CenterZ=0 NormalX=0 NormalY=0 NormalZ=1 AngleXU=0 Radius=1.5 StartAngle=4.71239 EndAngle=7.85398
    g13: ArcOfCircle CenterX=-1.5 CenterY=62 CenterZ=0 NormalX=0 NormalY=0 NormalZ=1 AngleXU=0 Radius=1.5 StartAngle=4.71239 EndAngle=7.85398
    g14: ArcOfCircle CenterX=-1.5 CenterY=56.25 CenterZ=0 NormalX=0 NormalY=0 NormalZ=1 AngleXU=0 Radius=1.5 StartAngle=4.71239 EndAngle=7.85398
    g15: ArcOfCircle CenterX=-11.49 CenterY=50.5 CenterZ=0 NormalX=0 NormalY=0 NormalZ=1 AngleXU=0 Radius=1.5 StartAngle=4.71239 EndAngle=7.85398
    g16: ArcOfCircle CenterX=-16.28 CenterY=44.75 CenterZ=0 NormalX=0 NormalY=0 NormalZ=1 AngleXU=0 Radius=1.5 StartAngle=4.71239 EndAngle=7.85398
    g17: ArcOfCircle CenterX=-18.2337 CenterY=39 CenterZ=0 NormalX=0 NormalY=0 NormalZ=1 AngleXU=0 Radius=1.5 StartAngle=4.71485 EndAngle=7.85398
    g18: ArcOfCircle CenterX=-16.2837 CenterY=27.25 CenterZ=0 NormalX=0 NormalY=0 NormalZ=1 AngleXU=0 Radius=1.5 StartAngle=4.71485 EndAngle=7.85398
    g19: ArcOfCircle CenterX=-18.2337 CenterY=33 CenterZ=0 NormalX=0 NormalY=0 NormalZ=1 AngleXU=0 Radius=1.5 StartAngle=4.71485 EndAngle=7.85398
    g20: ArcOfCircle CenterX=-11.49 CenterY=21.5 CenterZ=0 NormalX=0 NormalY=0 NormalZ=1 AngleXU=0 Radius=1.5 StartAngle=4.71239 EndAngle=7.85398
    g21: ArcOfCircle CenterX=-1.5 CenterY=4.25 CenterZ=0 NormalX=0 NormalY=0 NormalZ=1 AngleXU=0 Radius=1.5 StartAngle=4.71239 EndAngle=7.85398
    g22: ArcOfCircle CenterX=-1.5 CenterY=10 CenterZ=0 NormalX=0 NormalY=0 NormalZ=1 AngleXU=0 Radius=1.5 StartAngle=4.71239 EndAngle=7.85398
    g23: ArcOfCircle CenterX=-1.5 CenterY=15.75 CenterZ=0 NormalX=0 NormalY=0 NormalZ=1 AngleXU=0 Radius=1.5 StartAngle=4.71239 EndAngle=7.85398
    g24: LineSegment StartX=-49.19 StartY=69.25 StartZ=0 EndX=-1.5 EndY=69.25 EndZ=0
    g25: LineSegment StartX=-49.19 StartY=66.25 StartZ=0 EndX=-1.5 EndY=66.25 EndZ=0
    g26: LineSegment StartX=-49.19 StartY=63.5 StartZ=0 EndX=-1.5 EndY=63.5 EndZ=0
    g27: LineSegment StartX=-49.19 StartY=60.5 StartZ=0 EndX=-1.5 EndY=60.5 EndZ=0
    g28: LineSegment StartX=-49.19 StartY=57.75 StartZ=0 EndX=-1.5 EndY=57.75 EndZ=0
    g29: LineSegment StartX=-49.19 StartY=54.75 StartZ=0 EndX=-1.5 EndY=54.75 EndZ=0
    g30: LineSegment StartX=-49.19 StartY=52 StartZ=0 EndX=-11.49 EndY=52 EndZ=0
    g31: LineSegment StartX=-49.19 StartY=49 StartZ=0 EndX=-11.49 EndY=49 EndZ=0
    g32: LineSegment StartX=-49.19 StartY=46.25 StartZ=0 EndX=-16.28 EndY=46.25 EndZ=0
    g33: LineSegment StartX=-49.19 StartY=43.25 StartZ=0 EndX=-16.28 EndY=43.25 EndZ=0
    g34: LineSegment StartX=-49.19 StartY=40.5 StartZ=0 EndX=-18.2337 EndY=40.5 EndZ=0
    g35: LineSegment StartX=-49.19 StartY=37.5 StartZ=0 EndX=-18.23 EndY=37.5 EndZ=0
    g36: LineSegment StartX=-49.19 StartY=34.5 StartZ=0 EndX=-18.2337 EndY=34.5 EndZ=0
    g37: LineSegment StartX=-49.19 StartY=31.5 StartZ=0 EndX=-18.23 EndY=31.5 EndZ=0
    g38: LineSegment StartX=-49.19 StartY=28.75 StartZ=0 EndX=-16.2837 EndY=28.75 EndZ=0
    g39: LineSegment StartX=-49.19 StartY=25.75 StartZ=0 EndX=-16.28 EndY=25.75 EndZ=0
    g40: LineSegment StartX=-49.19 StartY=23 StartZ=0 EndX=-11.49 EndY=23 EndZ=0
    g41: LineSegment StartX=-49.19 StartY=20 StartZ=0 EndX=-11.49 EndY=20 EndZ=0
    g42: LineSegment StartX=-49.19 StartY=17.25 StartZ=0 EndX=-1.5 EndY=17.25 EndZ=0
    g43: LineSegment StartX=-49.19 StartY=14.25 StartZ=0 EndX=-1.5 EndY=14.25 EndZ=0
    g44: LineSegment StartX=-49.19 StartY=11.5 StartZ=0 EndX=-1.5 EndY=11.5 EndZ=0
    g45: LineSegment StartX=-49.19 StartY=8.5 StartZ=0 EndX=-1.5 EndY=8.5 EndZ=0
    g46: LineSegment StartX=-49.19 StartY=5.75 StartZ=0 EndX=-1.5 EndY=5.75 EndZ=0
    g47: LineSegment StartX=-49.19 StartY=2.75 StartZ=0 EndX=-1.5 EndY=2.75 EndZ=0
  constraints (120):
    c: Vertical(g0)
    c: Distance(g0) = 3
    c: Block(g0)
    c: Vertical(g1)
    c: Distance(g1) = 3
    c: Vertical(g2)
    c: Equal(g0,g2) = 3
    c: Block(g2)
    c: Vertical(g3)
    c: Equal(g1,g3) = 3
    c: Vertical(g4)
    c: Equal(g0,g4) = 3
    c: Block(g4)
    c: Vertical(g5)
    c: Equal(g1,g5) = 3
    c: Vertical(g6)
    c: Equal(g0,g6) = 3
    c: Block(g6)
    c: Vertical(g7)
    c: Equal(g1,g7) = 3
    c: Vertical(g8)
    c: Equal(g0,g8) = 3
    c: Block(g8)
    c: Vertical(g9)
    c: Equal(g1,g9) = 3
    c: Vertical(g10)
    c: Equal(g0,g10) = 3
    c: Block(g10)
    c: Vertical(g11)
    c: Equal(g1,g11) = 3
    c: Block(g12)
    c: Block(g13)
    c: Block(g14)
    c: Block(g15)
    c: Block(g16)
    c: Block(g17)
    c: Block(g18)
    c: Block(g19)
    c: Block(g20)
    c: Block(g21)
    c: Block(g22)
    c: Block(g23)
    c: Block(g11)
    c: Block(g9)
    c: Block(g7)
    c: Block(g5)
    c: Block(g3)
    c: Block(g1)
    c: Coincident(g24,g0)
    c: Coincident(g24,g12)
    c: Horizontal(g24)
    c: Coincident(g25,g0)
    c: Coincident(g25,g12)
    c: Horizontal(g25)
    c: Coincident(g26,g1)
    c: Coincident(g26,g13)
    c: Horizontal(g26)
    c: Coincident(g27,g1)
    c: Coincident(g27,g13)
    c: Horizontal(g27)
    c: Coincident(g28,g2)
    c: Coincident(g28,g14)
    c: Horizontal(g28)
    c: Coincident(g29,g2)
    c: Coincident(g29,g14)
    c: Horizontal(g29)
    c: Coincident(g30,g3)
    c: Coincident(g30,g15)
    c: Horizontal(g30)
    c: Coincident(g31,g3)
    c: Coincident(g31,g15)
    c: Horizontal(g31)
    c: Coincident(g32,g4)
    c: Coincident(g32,g16)
    c: Horizontal(g32)
    c: Coincident(g33,g4)
    c: Coincident(g33,g16)
    c: Horizontal(g33)
    c: Coincident(g34,g5)
    c: Coincident(g34,g17)
    c: Horizontal(g34)
    c: Coincident(g35,g5)
    c: Coincident(g35,g17)
    c: Horizontal(g35)
    c: Coincident(g36,g6)
    c: Coincident(g36,g19)
    c: Horizontal(g36)
    c: Coincident(g37,g6)
    c: Coincident(g37,g19)
    c: Horizontal(g37)
    c: Coincident(g38,g7)
    c: Coincident(g38,g18)
    c: Horizontal(g38)
    c: Coincident(g39,g7)
    c: Coincident(g39,g18)
    c: Horizontal(g39)
    c: Coincident(g40,g8)
    c: Coincident(g40,g20)
    c: Horizontal(g40)
    c: Coincident(g41,g8)
    c: Coincident(g41,g20)
    c: Horizontal(g41)
    c: Coincident(g42,g9)
    c: Coincident(g42,g23)
    c: Horizontal(g42)
    c: Coincident(g43,g9)
    c: Coincident(g43,g23)
    c: Horizontal(g43)
    c: Coincident(g44,g10)
    c: Coincident(g44,g22)
    c: Horizontal(g44)
    c: Coincident(g45,g10)
    c: Coincident(g45,g22)
    c: Horizontal(g45)
    c: Coincident(g46,g11)
    c: Coincident(g46,g21)
    c: Horizontal(g46)
    c: Coincident(g47,g11)
    c: Coincident(g47,g21)
    c: Horizontal(g47)
FEATURE [Sketcher::SketchObject] Sketch031
  FullyConstrained = true
  Placement = pos=(117,19,0) rot=(0.57735,0.57735,0.57735;2.0944rad)
  sketch-geometry (24):
    g0: ArcOfCircle CenterX=-49.19 CenterY=67.75 CenterZ=0 NormalX=0 NormalY=0 NormalZ=1 AngleXU=0 Radius=1.5 StartAngle=1.5708 EndAngle=4.71239
    g1: ArcOfCircle CenterX=-49.19 CenterY=62 CenterZ=0 NormalX=0 NormalY=0 NormalZ=1 AngleXU=0 Radius=1.5 StartAngle=1.5708 EndAngle=4.71239
    g2: ArcOfCircle CenterX=-49.19 CenterY=56.25 CenterZ=0 NormalX=0 NormalY=0 NormalZ=1 AngleXU=0 Radius=1.5 StartAngle=1.5708 EndAngle=4.71239
    g3: ArcOfCircle CenterX=-49.19 CenterY=50.5 CenterZ=0 NormalX=0 NormalY=0 NormalZ=1 AngleXU=0 Radius=1.5 StartAngle=1.5708 EndAngle=4.71239
    g4: ArcOfCircle CenterX=-49.19 CenterY=44.75 CenterZ=0 NormalX=0 NormalY=0 NormalZ=1 AngleXU=0 Radius=1.5 StartAngle=1.5708 EndAngle=4.71239
    g5: ArcOfCircle CenterX=-49.19 CenterY=39 CenterZ=0 NormalX=0 NormalY=0 NormalZ=1 AngleXU=0 Radius=1.5 StartAngle=1.5708 EndAngle=4.71239
    g6: ArcOfCircle CenterX=-49.19 CenterY=33 CenterZ=0 NormalX=0 NormalY=0 NormalZ=1 AngleXU=0 Radius=1.5 StartAngle=1.5708 EndAngle=4.71239
    g7: ArcOfCircle CenterX=-49.19 CenterY=27.25 CenterZ=0 NormalX=0 NormalY=0 NormalZ=1 AngleXU=0 Radius=1.5 StartAngle=1.5708 EndAngle=4.71239
    g8: ArcOfCircle CenterX=-49.19 CenterY=21.5 CenterZ=0 NormalX=0 NormalY=0 NormalZ=1 AngleXU=0 Radius=1.5 StartAngle=1.5708 EndAngle=4.71239
    g9: ArcOfCircle CenterX=-49.19 CenterY=15.75 CenterZ=0 NormalX=0 NormalY=0 NormalZ=1 AngleXU=0 Radius=1.5 StartAngle=1.5708 EndAngle=4.71239
    g10: ArcOfCircle CenterX=-49.19 CenterY=10 CenterZ=0 NormalX=0 NormalY=0 NormalZ=1 AngleXU=0 Radius=1.5 StartAngle=1.5708 EndAngle=4.71239
    g11: ArcOfCircle CenterX=-49.19 CenterY=4.25 CenterZ=0 NormalX=0 NormalY=0 NormalZ=1 AngleXU=0 Radius=1.5 StartAngle=1.5708 EndAngle=4.71239
    g12: LineSegment StartX=-49.19 StartY=69.25 StartZ=0 EndX=-49.19 EndY=66.25 EndZ=0
    g13: LineSegment StartX=-49.19 StartY=63.5 StartZ=0 EndX=-49.19 EndY=60.5 EndZ=0
    g14: LineSegment StartX=-49.19 StartY=57.75 StartZ=0 EndX=-49.19 EndY=54.75 EndZ=0
    g15: LineSegment StartX=-49.19 StartY=52 StartZ=0 EndX=-49.19 EndY=49 EndZ=0
    g16: LineSegment StartX=-49.19 StartY=46.25 StartZ=0 EndX=-49.19 EndY=43.25 EndZ=0
    g17: LineSegment StartX=-49.19 StartY=40.5 StartZ=0 EndX=-49.19 EndY=37.5 EndZ=0
    g18: LineSegment StartX=-49.19 StartY=34.5 StartZ=0 EndX=-49.19 EndY=31.5 EndZ=0
    g19: LineSegment StartX=-49.19 StartY=28.75 StartZ=0 EndX=-49.19 EndY=25.75 EndZ=0
    g20: LineSegment StartX=-49.19 StartY=23 StartZ=0 EndX=-49.19 EndY=20 EndZ=0
    g21: LineSegment StartX=-49.19 StartY=17.25 StartZ=0 EndX=-49.19 EndY=14.25 EndZ=0
    g22: LineSegment StartX=-49.19 StartY=11.5 StartZ=0 EndX=-49.19 EndY=8.5 EndZ=0
    g23: LineSegment StartX=-49.19 StartY=5.75 StartZ=0 EndX=-49.19 EndY=2.75 EndZ=0
  constraints (48):
    c: Block(g0)
    c: Block(g1)
    c: Block(g2)
    c: Block(g3)
    c: Block(g4)
    c: Block(g5)
    c: Block(g6)
    c: Block(g7)
    c: Block(g8)
    c: Block(g9)
    c: Block(g10)
    c: Block(g11)
    c: Coincident(g12,g0)
    c: Coincident(g12,g0)
    c: Vertical(g12)
    c: Vertical(g13)
    c: Coincident(g13,g1)
    c: Vertical(g14)
    c: Coincident(g14,g2)
    c: Vertical(g15)
    c: Coincident(g15,g3)
    c: Vertical(g16)
    c: Coincident(g16,g4)
    c: Vertical(g17)
    c: Coincident(g17,g5)
    c: Vertical(g18)
    c: Coincident(g18,g6)
    c: Vertical(g19)
    c: Coincident(g19,g7)
    c: Vertical(g20)
    c: Coincident(g20,g8)
    c: Vertical(g21)
    c: Coincident(g21,g9)
    c: Vertical(g22)
    c: Coincident(g22,g10)
    c: Vertical(g23)
    c: Coincident(g23,g11)
    c: Block(g23)
    c: Block(g22)
    c: Block(g21)
    c: Block(g20)
    c: Block(g13)
    c: Block(g14)
    c: Block(g15)
    c: Block(g16)
    c: Block(g17)
    c: Block(g18)
    c: Block(g19)
FEATURE [Part::Extrusion] Extrude022
  Base = -> Sketch030
  Dir = (1,-2e-16,2e-16)
  DirMode = 2
  FaceMakerClass = Part::FaceMakerBullseye
  LengthFwd = 19
  LengthRev = 0
  Placement = pos=(-19,0,0) rot=(0,0,1;0rad)
  Solid = true
  Symmetric = false
FEATURE [Part::Fillet] Fillet022
  Base = -> Extrude022
  Edges = 24 edges r=1.49: [Edge6,Edge11,Edge18,Edge23,Edge30,Edge35,Edge42,Edge47,Edge54,Edge59,Edge66,Edge71,Edge78,Edge83,Edge90,Edge95,Edge102,Edge107,Edge114,Edge119,Edge126,Edge131,Edge138,Edge143]
FEATURE [Part::Cut] Cut020  label="top010"
  Base = -> Cut019
  Tool = -> Fillet022
FEATURE [Sketcher::SketchObject] Sketch032
  FullyConstrained = true
  Placement = pos=(117,19,0) rot=(0.57735,0.57735,0.57735;2.0944rad)
  sketch-geometry (48):
    g0: LineSegment StartX=-49.19 StartY=69.25 StartZ=0 EndX=-49.19 EndY=66.25 EndZ=0
    g1: LineSegment StartX=-49.19 StartY=63.5 StartZ=0 EndX=-49.19 EndY=60.5 EndZ=0
    g2: LineSegment StartX=-49.19 StartY=57.75 StartZ=0 EndX=-49.19 EndY=54.75 EndZ=0
    g3: LineSegment StartX=-49.19 StartY=52 StartZ=0 EndX=-49.19 EndY=49 EndZ=0
    g4: LineSegment StartX=-49.19 StartY=46.25 StartZ=0 EndX=-49.19 EndY=43.25 EndZ=0
    g5: LineSegment StartX=-49.19 StartY=40.5 StartZ=0 EndX=-49.19 EndY=37.5 EndZ=0
    g6: LineSegment StartX=-49.19 StartY=34.5 StartZ=0 EndX=-49.19 EndY=31.5 EndZ=0
    g7: LineSegment StartX=-49.19 StartY=28.75 StartZ=0 EndX=-49.19 EndY=25.75 EndZ=0
    g8: LineSegment StartX=-49.19 StartY=23 StartZ=0 EndX=-49.19 EndY=20 EndZ=0
    g9: LineSegment StartX=-49.19 StartY=17.25 StartZ=0 EndX=-49.19 EndY=14.25 EndZ=0
    g10: LineSegment StartX=-49.19 StartY=11.5 StartZ=0 EndX=-49.19 EndY=8.5 EndZ=0
    g11: LineSegment StartX=-49.19 StartY=5.75 StartZ=0 EndX=-49.19 EndY=2.75 EndZ=0
    g12: ArcOfCircle CenterX=-1.5 CenterY=67.75 CenterZ=0 NormalX=0 NormalY=0 NormalZ=1 AngleXU=0 Radius=1.5 StartAngle=4.71239 EndAngle=7.85398
    g13: ArcOfCircle CenterX=-1.5 CenterY=62 CenterZ=0 NormalX=0 NormalY=0 NormalZ=1 AngleXU=0 Radius=1.5 StartAngle=4.71239 EndAngle=7.85398
    g14: ArcOfCircle CenterX=-1.5 CenterY=56.25 CenterZ=0 NormalX=0 NormalY=0 NormalZ=1 AngleXU=0 Radius=1.5 StartAngle=4.71239 EndAngle=7.85398
    g15: ArcOfCircle CenterX=-11.49 CenterY=50.5 CenterZ=0 NormalX=0 NormalY=0 NormalZ=1 AngleXU=0 Radius=1.5 StartAngle=4.71239 EndAngle=7.85398
    g16: ArcOfCircle CenterX=-16.28 CenterY=44.75 CenterZ=0 NormalX=0 NormalY=0 NormalZ=1 AngleXU=0 Radius=1.5 StartAngle=4.71239 EndAngle=7.85398
    g17: ArcOfCircle CenterX=-18.2337 CenterY=39 CenterZ=0 NormalX=0 NormalY=0 NormalZ=1 AngleXU=0 Radius=1.5 StartAngle=4.71485 EndAngle=7.85398
    g18: ArcOfCircle CenterX=-16.2837 CenterY=27.25 CenterZ=0 NormalX=0 NormalY=0 NormalZ=1 AngleXU=0 Radius=1.5 StartAngle=4.71485 EndAngle=7.85398
    g19: ArcOfCircle CenterX=-18.2337 CenterY=33 CenterZ=0 NormalX=0 NormalY=0 NormalZ=1 AngleXU=0 Radius=1.5 StartAngle=4.71485 EndAngle=7.85398
    g20: ArcOfCircle CenterX=-11.49 CenterY=21.5 CenterZ=0 NormalX=0 NormalY=0 NormalZ=1 AngleXU=0 Radius=1.5 StartAngle=4.71239 EndAngle=7.85398
    g21: ArcOfCircle CenterX=-1.5 CenterY=4.25 CenterZ=0 NormalX=0 NormalY=0 NormalZ=1 AngleXU=0 Radius=1.5 StartAngle=4.71239 EndAngle=7.85398
    g22: ArcOfCircle CenterX=-1.5 CenterY=10 CenterZ=0 NormalX=0 NormalY=0 NormalZ=1 AngleXU=0 Radius=1.5 StartAngle=4.71239 EndAngle=7.85398
    g23: ArcOfCircle CenterX=-1.5 CenterY=15.75 CenterZ=0 NormalX=0 NormalY=0 NormalZ=1 AngleXU=0 Radius=1.5 StartAngle=4.71239 EndAngle=7.85398
    g24: LineSegment StartX=-49.19 StartY=69.25 StartZ=0 EndX=-1.5 EndY=69.25 EndZ=0
    g25: LineSegment StartX=-49.19 StartY=66.25 StartZ=0 EndX=-1.5 EndY=66.25 EndZ=0
    g26: LineSegment StartX=-49.19 StartY=63.5 StartZ=0 EndX=-1.5 EndY=63.5 EndZ=0
    g27: LineSegment StartX=-49.19 StartY=60.5 StartZ=0 EndX=-1.5 EndY=60.5 EndZ=0
    g28: LineSegment StartX=-49.19 StartY=57.75 StartZ=0 EndX=-1.5 EndY=57.75 EndZ=0
    g29: LineSegment StartX=-49.19 StartY=54.75 StartZ=0 EndX=-1.5 EndY=54.75 EndZ=0
    g30: LineSegment StartX=-49.19 StartY=52 StartZ=0 EndX=-11.49 EndY=52 EndZ=0
    g31: LineSegment StartX=-49.19 StartY=49 StartZ=0 EndX=-11.49 EndY=49 EndZ=0
    g32: LineSegment StartX=-49.19 StartY=46.25 StartZ=0 EndX=-16.28 EndY=46.25 EndZ=0
    g33: LineSegment StartX=-49.19 StartY=43.25 StartZ=0 EndX=-16.28 EndY=43.25 EndZ=0
    g34: LineSegment StartX=-49.19 StartY=40.5 StartZ=0 EndX=-18.2337 EndY=40.5 EndZ=0
    g35: LineSegment StartX=-49.19 StartY=37.5 StartZ=0 EndX=-18.23 EndY=37.5 EndZ=0
    g36: LineSegment StartX=-49.19 StartY=34.5 StartZ=0 EndX=-18.2337 EndY=34.5 EndZ=0
    g37: LineSegment StartX=-49.19 StartY=31.5 StartZ=0 EndX=-18.23 EndY=31.5 EndZ=0
    g38: LineSegment StartX=-49.19 StartY=28.75 StartZ=0 EndX=-16.2837 EndY=28.75 EndZ=0
    g39: LineSegment StartX=-49.19 StartY=25.75 StartZ=0 EndX=-16.28 EndY=25.75 EndZ=0
    g40: LineSegment StartX=-49.19 StartY=23 StartZ=0 EndX=-11.49 EndY=23 EndZ=0
    g41: LineSegment StartX=-49.19 StartY=20 StartZ=0 EndX=-11.49 EndY=20 EndZ=0
    g42: LineSegment StartX=-49.19 StartY=17.25 StartZ=0 EndX=-1.5 EndY=17.25 EndZ=0
    g43: LineSegment StartX=-49.19 StartY=14.25 StartZ=0 EndX=-1.5 EndY=14.25 EndZ=0
    g44: LineSegment StartX=-49.19 StartY=11.5 StartZ=0 EndX=-1.5 EndY=11.5 EndZ=0
    g45: LineSegment StartX=-49.19 StartY=8.5 StartZ=0 EndX=-1.5 EndY=8.5 EndZ=0
    g46: LineSegment StartX=-49.19 StartY=5.75 StartZ=0 EndX=-1.5 EndY=5.75 EndZ=0
    g47: LineSegment StartX=-49.19 StartY=2.75 StartZ=0 EndX=-1.5 EndY=2.75 EndZ=0
  constraints (120):
    c: Vertical(g0)
    c: Distance(g0) = 3
    c: Block(g0)
    c: Vertical(g1)
    c: Distance(g1) = 3
    c: Vertical(g2)
    c: Equal(g0,g2) = 3
    c: Block(g2)
    c: Vertical(g3)
    c: Equal(g1,g3) = 3
    c: Vertical(g4)
    c: Equal(g0,g4) = 3
    c: Block(g4)
    c: Vertical(g5)
    c: Equal(g1,g5) = 3
    c: Vertical(g6)
    c: Equal(g0,g6) = 3
    c: Block(g6)
    c: Vertical(g7)
    c: Equal(g1,g7) = 3
    c: Vertical(g8)
    c: Equal(g0,g8) = 3
    c: Block(g8)
    c: Vertical(g9)
    c: Equal(g1,g9) = 3
    c: Vertical(g10)
    c: Equal(g0,g10) = 3
    c: Block(g10)
    c: Vertical(g11)
    c: Equal(g1,g11) = 3
    c: Block(g12)
    c: Block(g13)
    c: Block(g14)
    c: Block(g15)
    c: Block(g16)
    c: Block(g17)
    c: Block(g18)
    c: Block(g19)
    c: Block(g20)
    c: Block(g21)
    c: Block(g22)
    c: Block(g23)
    c: Block(g11)
    c: Block(g9)
    c: Block(g7)
    c: Block(g5)
    c: Block(g3)
    c: Block(g1)
    c: Coincident(g24,g0)
    c: Coincident(g24,g12)
    c: Horizontal(g24)
    c: Coincident(g25,g0)
    c: Coincident(g25,g12)
    c: Horizontal(g25)
    c: Coincident(g26,g1)
    c: Coincident(g26,g13)
    c: Horizontal(g26)
    c: Coincident(g27,g1)
    c: Coincident(g27,g13)
    c: Horizontal(g27)
    c: Coincident(g28,g2)
    c: Coincident(g28,g14)
    c: Horizontal(g28)
    c: Coincident(g29,g2)
    c: Coincident(g29,g14)
    c: Horizontal(g29)
    c: Coincident(g30,g3)
    c: Coincident(g30,g15)
    c: Horizontal(g30)
    c: Coincident(g31,g3)
    c: Coincident(g31,g15)
    c: Horizontal(g31)
    c: Coincident(g32,g4)
    c: Coincident(g32,g16)
    c: Horizontal(g32)
    c: Coincident(g33,g4)
    c: Coincident(g33,g16)
    c: Horizontal(g33)
    c: Coincident(g34,g5)
    c: Coincident(g34,g17)
    c: Horizontal(g34)
    c: Coincident(g35,g5)
    c: Coincident(g35,g17)
    c: Horizontal(g35)
    c: Coincident(g36,g6)
    c: Coincident(g36,g19)
    c: Horizontal(g36)
    c: Coincident(g37,g6)
    c: Coincident(g37,g19)
    c: Horizontal(g37)
    c: Coincident(g38,g7)
    c: Coincident(g38,g18)
    c: Horizontal(g38)
    c: Coincident(g39,g7)
    c: Coincident(g39,g18)
    c: Horizontal(g39)
    c: Coincident(g40,g8)
    c: Coincident(g40,g20)
    c: Horizontal(g40)
    c: Coincident(g41,g8)
    c: Coincident(g41,g20)
    c: Horizontal(g41)
    c: Coincident(g42,g9)
    c: Coincident(g42,g23)
    c: Horizontal(g42)
    c: Coincident(g43,g9)
    c: Coincident(g43,g23)
    c: Horizontal(g43)
    c: Coincident(g44,g10)
    c: Coincident(g44,g22)
    c: Horizontal(g44)
    c: Coincident(g45,g10)
    c: Coincident(g45,g22)
    c: Horizontal(g45)
    c: Coincident(g46,g11)
    c: Coincident(g46,g21)
    c: Horizontal(g46)
    c: Coincident(g47,g11)
    c: Coincident(g47,g21)
    c: Horizontal(g47)
FEATURE [Part::Extrusion] Extrude023
  Base = -> Sketch032
  Dir = (1,-2e-16,2e-16)
  DirMode = 2
  FaceMakerClass = Part::FaceMakerBullseye
  LengthFwd = 19
  LengthRev = 0
  Placement = pos=(-19,0,0) rot=(0,0,1;0rad)
  Solid = true
  Symmetric = false
FEATURE [Part::Fillet] Fillet023
  Base = -> Extrude023
  Edges = 24 edges r=1.49: [Edge6,Edge11,Edge18,Edge23,Edge30,Edge35,Edge42,Edge47,Edge54,Edge59,Edge66,Edge71,Edge78,Edge83,Edge90,Edge95,Edge102,Edge107,Edge114,Edge119,Edge126,Edge131,Edge138,Edge143]
  Placement = pos=(0,0.05,0) rot=(0,0,1;0rad)
FEATURE [Part::Cut] Cut014  label="bottom003"
  Base = -> Cut007
  Tool = -> Fusion047
FEATURE [Part::Cut] Cut021  label="bottom004"
  Base = -> Cut014
  Tool = -> Fillet023
FEATURE [Sketcher::SketchObject] Sketch033
  FullyConstrained = true
  Placement = pos=(117,19,0) rot=(0.57735,0.57735,0.57735;2.0944rad)
  sketch-geometry (8):
    g0: LineSegment StartX=-49.19 StartY=69.25 StartZ=0 EndX=-49.19 EndY=66.25 EndZ=0
    g1: LineSegment StartX=-49.19 StartY=5.75 StartZ=0 EndX=-49.19 EndY=2.75 EndZ=0
    g2: ArcOfCircle CenterX=-1.5 CenterY=67.75 CenterZ=0 NormalX=0 NormalY=0 NormalZ=1 AngleXU=0 Radius=1.5 StartAngle=4.71239 EndAngle=7.85398
    g3: ArcOfCircle CenterX=-1.5 CenterY=4.25 CenterZ=0 NormalX=0 NormalY=0 NormalZ=1 AngleXU=0 Radius=1.5 StartAngle=4.71239 EndAngle=7.85398
    g4: LineSegment StartX=-49.19 StartY=69.25 StartZ=0 EndX=-1.5 EndY=69.25 EndZ=0
    g5: LineSegment StartX=-49.19 StartY=66.25 StartZ=0 EndX=-1.5 EndY=66.25 EndZ=0
    g6: LineSegment StartX=-49.19 StartY=5.75 StartZ=0 EndX=-1.5 EndY=5.75 EndZ=0
    g7: LineSegment StartX=-49.19 StartY=2.75 StartZ=0 EndX=-1.5 EndY=2.75 EndZ=0
  constraints (19):
    c: Vertical(g0)
    c: Distance(g0) = 3
    c: Block(g0)
    c: Vertical(g1)
    c: Block(g2)
    c: Block(g3)
    c: Block(g1)
    c: Coincident(g4,g0)
    c: Coincident(g4,g2)
    c: Horizontal(g4)
    c: Coincident(g5,g0)
    c: Coincident(g5,g2)
    c: Horizontal(g5)
    c: Coincident(g6,g1)
    c: Coincident(g6,g3)
    c: Horizontal(g6)
    c: Coincident(g7,g1)
    c: Coincident(g7,g3)
    c: Horizontal(g7)
FEATURE [Sketcher::SketchObject] Sketch034
  FullyConstrained = true
  Placement = pos=(117,19,0) rot=(0.57735,0.57735,0.57735;2.0944rad)
  sketch-geometry (8):
    g0: LineSegment StartX=-49.19 StartY=63.5 StartZ=0 EndX=-49.19 EndY=60.5 EndZ=0
    g1: LineSegment StartX=-49.19 StartY=11.5 StartZ=0 EndX=-49.19 EndY=8.5 EndZ=0
    g2: ArcOfCircle CenterX=-1.5 CenterY=62 CenterZ=0 NormalX=0 NormalY=0 NormalZ=1 AngleXU=0 Radius=1.5 StartAngle=4.71239 EndAngle=7.85398
    g3: ArcOfCircle CenterX=-1.5 CenterY=10 CenterZ=0 NormalX=0 NormalY=0 NormalZ=1 AngleXU=0 Radius=1.5 StartAngle=4.71239 EndAngle=7.85398
    g4: LineSegment StartX=-49.19 StartY=63.5 StartZ=0 EndX=-1.5 EndY=63.5 EndZ=0
    g5: LineSegment StartX=-49.19 StartY=60.5 StartZ=0 EndX=-1.5 EndY=60.5 EndZ=0
    g6: LineSegment StartX=-49.19 StartY=11.5 StartZ=0 EndX=-1.5 EndY=11.5 EndZ=0
    g7: LineSegment StartX=-49.19 StartY=8.5 StartZ=0 EndX=-1.5 EndY=8.5 EndZ=0
  constraints (19):
    c: Vertical(g0)
    c: Distance(g0) = 3
    c: Vertical(g1)
    c: Block(g1)
    c: Block(g2)
    c: Block(g3)
    c: Block(g0)
    c: Coincident(g4,g0)
    c: Coincident(g4,g2)
    c: Horizontal(g4)
    c: Coincident(g5,g0)
    c: Coincident(g5,g2)
    c: Horizontal(g5)
    c: Coincident(g6,g1)
    c: Coincident(g6,g3)
    c: Horizontal(g6)
    c: Coincident(g7,g1)
    c: Coincident(g7,g3)
    c: Horizontal(g7)
FEATURE [Part::Extrusion] Extrude024
  Base = -> Sketch033
  Dir = (1,0,0)
  DirMode = 2
  FaceMakerClass = Part::FaceMakerBullseye
  LengthFwd = 10
  LengthRev = 0
  Solid = true
  Symmetric = false
FEATURE [Part::Extrusion] Extrude025
  Base = -> Sketch034
  Dir = (1,0,0)
  DirMode = 2
  FaceMakerClass = Part::FaceMakerBullseye
  LengthFwd = 10
  LengthRev = 0
  Solid = true
  Symmetric = false
FEATURE [Part::Fillet] Fillet024  label="removeFromtMoreFrontCaseScrewRetainers"
  Base = -> Extrude024
  Edges = 4 edges r=1.49: [Edge6,Edge11,Edge18,Edge23]
  Placement = pos=(-11,0,0) rot=(0,0,1;0rad)
FEATURE [Part::Fillet] Fillet025  label="removeFromtMoreFrontCaseScrewRetainers001"
  Base = -> Extrude025
  Edges = 4 edges r=1.49: [Edge6,Edge11,Edge18,Edge23]
  Placement = pos=(-19,0,0) rot=(0,0,1;0rad)
FEATURE [Part::Cut] Cut022
  Base = -> Cut015
  Tool = -> Fillet025
FEATURE [Part::Cut] Cut023  label="screwRetainers"
  Base = -> Cut022
  Tool = -> Fillet024
FEATURE [Part::MultiFuse] Fusion056  label="bottom005"
  Shapes = -> [Fusion044,Cut021]
FEATURE [Part::MultiFuse] Fusion057  label="casePillars001"
  Shapes = -> [Cut016,Fusion052]
FEATURE [Part::MultiFuse] Fusion058  label="bottom006"
  Shapes = -> [Fusion056,Cut023]
FEATURE [Part::MultiFuse] Fusion059  label="bottom007"
  Shapes = -> [Fusion058,Fillet005]
FEATURE [Part::MultiFuse] Fusion060  label="bottom008"
  Shapes = -> [Fusion059,Fusion]
FEATURE [Part::MultiFuse] Fusion061  label="top011"
  Shapes = -> [Cut006,Cut020]
FEATURE [Part::MultiFuse] Fusion062  label="top012"
  Shapes = -> [Fusion057,Fusion061]
FEATURE [Sketcher::SketchObject] Sketch035  label="topSketch007"
  FullyConstrained = true
  sketch-geometry (6):
    g0: LineSegment StartX=19 StartY=38 StartZ=0 EndX=117 EndY=38 EndZ=0
    g1: ArcOfCircle CenterX=19 CenterY=19 CenterZ=0 NormalX=0 NormalY=0 NormalZ=1 AngleXU=0 Radius=19 StartAngle=1.5708 EndAngle=3.14159
    g2: LineSegment StartX=117 StartY=38 StartZ=0 EndX=117 EndY=19 EndZ=0
    g3: LineSegment StartX=98 StartY=1.0161e-12 StartZ=0 EndX=5.22862e-06 EndY=1.0161e-12 EndZ=0
    g4: LineSegment StartX=5.22862e-06 StartY=19 StartZ=0 EndX=5.22862e-06 EndY=1.0161e-12 EndZ=0
    g5: ArcOfCircle CenterX=98 CenterY=19 CenterZ=0 NormalX=0 NormalY=0 NormalZ=1 AngleXU=0 Radius=19 StartAngle=4.71239 EndAngle=6.28319
  constraints (16):
    c: Horizontal(g0)
    c: Distance(g0) = 98
    c: Coincident(g1,g0)
    c: Block(g1)
    c: Coincident(g2,g0)
    c: Vertical(g2)
    c: Distance(g2) = 19
    c: Horizontal(g3)
    c: Coincident(g4,g1)
    c: Vertical(g4)
    c: Coincident(g3,g4)
    c: Block(g3)
    c: Coincident(g5,g2)
    c: Coincident(g5,g3)
    c: Block(g0)
    c: Block(g5)
FEATURE [Part::Extrusion] Extrude026  label="sideA001"
  Base = -> Sketch035
  Dir = (0,0,1)
  DirMode = 2
  FaceMakerClass = Part::FaceMakerBullseye
  LengthFwd = 3
  LengthRev = 0
  Placement = pos=(0,0,-2.7) rot=(0,0,1;0rad)
  Solid = true
  Symmetric = false
FEATURE [Sketcher::SketchObject] Sketch036  label="topSketch008"
  FullyConstrained = true
  sketch-geometry (6):
    g0: LineSegment StartX=19 StartY=38 StartZ=0 EndX=117 EndY=38 EndZ=0
    g1: ArcOfCircle CenterX=19 CenterY=19 CenterZ=0 NormalX=0 NormalY=0 NormalZ=1 AngleXU=0 Radius=19 StartAngle=1.5708 EndAngle=3.14159
    g2: LineSegment StartX=117 StartY=38 StartZ=0 EndX=117 EndY=19 EndZ=0
    g3: LineSegment StartX=98 StartY=1.0161e-12 StartZ=0 EndX=5.22862e-06 EndY=1.0161e-12 EndZ=0
    g4: LineSegment StartX=5.22862e-06 StartY=19 StartZ=0 EndX=5.22862e-06 EndY=1.0161e-12 EndZ=0
    g5: ArcOfCircle CenterX=98 CenterY=19 CenterZ=0 NormalX=0 NormalY=0 NormalZ=1 AngleXU=0 Radius=19 StartAngle=4.71239 EndAngle=6.28319
  constraints (16):
    c: Horizontal(g0)
    c: Distance(g0) = 98
    c: Coincident(g1,g0)
    c: Block(g1)
    c: Coincident(g2,g0)
    c: Vertical(g2)
    c: Distance(g2) = 19
    c: Horizontal(g3)
    c: Coincident(g4,g1)
    c: Vertical(g4)
    c: Coincident(g3,g4)
    c: Block(g3)
    c: Coincident(g5,g2)
    c: Coincident(g5,g3)
    c: Block(g0)
    c: Block(g5)
FEATURE [Part::Extrusion] Extrude027  label="sideB001"
  Base = -> Sketch036
  Dir = (0,0,1)
  DirMode = 2
  FaceMakerClass = Part::FaceMakerBullseye
  LengthFwd = 3
  LengthRev = 0
  Placement = pos=(0,0,71.7) rot=(0,0,1;0rad)
  Solid = true
  Symmetric = false
FEATURE [Part::MultiFuse] Fusion064  label="removeFromBottom"
  Shapes = -> [Extrude026,Extrude027]
FEATURE [Part::Cut] Cut024  label="bottom009"
  Base = -> Fusion060
  Tool = -> Fusion064
FEATURE [Sketcher::SketchObject] Sketch037  label="topSketch009"
  FullyConstrained = true
  sketch-geometry (6):
    g0: ArcOfCircle CenterX=19 CenterY=19 CenterZ=0 NormalX=0 NormalY=0 NormalZ=1 AngleXU=0 Radius=19 StartAngle=1.5708 EndAngle=3.14159
    g1: LineSegment StartX=5.22862e-06 StartY=19 StartZ=0 EndX=5.22862e-06 EndY=1.19904e-11 EndZ=0
    g2: LineSegment StartX=19 StartY=38 StartZ=0 EndX=124 EndY=38 EndZ=0
    g3: LineSegment StartX=5.22862e-06 StartY=1.19904e-11 StartZ=0 EndX=105 EndY=1.19904e-11 EndZ=0
    g4: ArcOfCircle CenterX=105 CenterY=19 CenterZ=0 NormalX=0 NormalY=0 NormalZ=1 AngleXU=0 Radius=19 StartAngle=4.71239 EndAngle=6.28319
    g5: LineSegment StartX=124 StartY=38 StartZ=0 EndX=124 EndY=19 EndZ=0
  constraints (16):
    c: Block(g0)
    c: Coincident(g1,g0)
    c: Vertical(g1)
    c: Horizontal(g2)
    c: Distance(g2) = 105
    c: Coincident(g2,g0)
    c: Distance(g1) = 19
    c: Coincident(g3,g1)
    c: Horizontal(g3)
    c: Distance(g3) = 105
    c: Block(g4)
    c: Coincident(g4,g3)
    c: Coincident(g5,g2)
    c: Coincident(g5,g4)
    c: Vertical(g5)
    c: Distance(g5) = 19
FEATURE [Part::Extrusion] Extrude028  label="sideB"
  Base = -> Sketch037
  Dir = (0,0,1)
  DirMode = 2
  FaceMakerClass = Part::FaceMakerBullseye
  LengthFwd = 3
  LengthRev = 0
  Placement = pos=(0,0,72) rot=(0,0,1;0rad)
  Solid = true
  Symmetric = false
